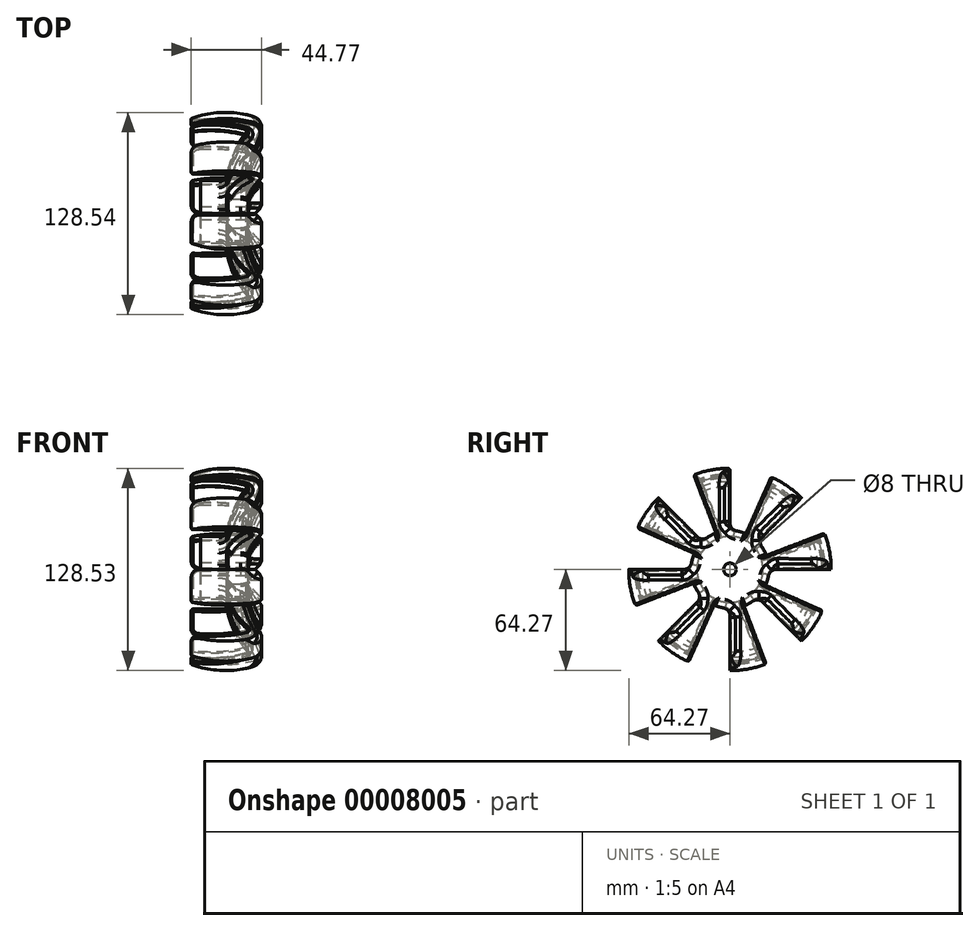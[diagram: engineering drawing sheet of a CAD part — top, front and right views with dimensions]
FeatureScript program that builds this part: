
annotation { "Feature Type Name" : "Feature", "Feature Type Description" : "" }
export const myFeature = defineFeature(function(context is Context, id is Id, definition is map)
    precondition{}
    {
        {
            var Q0;
            Q0=qCreatedBy(makeId("Front.planeOp"),FACE);
            var sketch = newSketch(context, id + "F0", { "sketchPlane" : qUnion([Q0])});
            skLineSegment(sketch, "E0", {"start": v(-28.32, 0) * mm, "end": v(30.34, 0) * mm, "construction": true});
            skLineSegment(sketch, "E1", {"start": v(-40.15, 4) * mm, "end": v(-10.15, 4) * mm});
            skLineSegment(sketch, "E2", {"start": v(-10.15, 4) * mm, "end": v(-10.15, 9.48) * mm});
            skLineSegment(sketch, "E3", {"start": v(-45.9, 60.38) * mm, "end": v(-45.9, 58.04) * mm});
            skLineSegment(sketch, "E4", {"start": v(-23.9, 20.95) * mm, "end": v(-40.15, 20.95) * mm});
            skLineSegment(sketch, "E5", {"start": v(-40.15, 20.95) * mm, "end": v(-40.15, 4) * mm});
            skArc(sketch, "E6", {"start": v(-6.27, 61.72) * mm, "mid": v(-26.2, 64.23) * mm, "end": v(-45.9, 60.38) * mm});
            skArc(sketch, "E7", {"start": v(-1.68, 52.13) * mm, "mid": v(-1.84, 57.95) * mm, "end": v(-6.27, 61.72) * mm});
            skArc(sketch, "E8", {"start": v(-1.68, 52.13) * mm, "mid": v(-8.01, 31.22) * mm, "end": v(-10.15, 9.48) * mm});
            skArc(sketch, "E9", {"start": v(-10.3, 52.56) * mm, "mid": v(-19.4, 37.75) * mm, "end": v(-23.9, 20.95) * mm});
            skArc(sketch, "E10", {"start": v(-10.98, 55.75) * mm, "mid": v(-28.31, 58.92) * mm, "end": v(-45.9, 58.04) * mm});
            skArc(sketch, "E11", {"start": v(-10.3, 52.56) * mm, "mid": v(-9.75, 54.35) * mm, "end": v(-10.98, 55.75) * mm});
            skSolve(sketch);
        }
        {
            var Q0;
            Q0 = qSketchRegion(id + "F0", true);
            var Q1;
            Q1=sQuery(id+"F0.wireOp",EDGE,"E0");
            revolve(context, id + "F1", {"entities" : qUnion([Q0]), "axis" : qUnion([Q1]), "revolveType" : RevolveType.FULL});
        }
        {
            var Q0;
            Q0=qCreatedBy(makeId("Right.planeOp"),FACE);
            var sketch = newSketch(context, id + "F2", { "sketchPlane" : qUnion([Q0])});
            skCircle(sketch, "E12", {"center": v(0, 0) * mm, "radius": 24.84 * mm});
            skLineSegment(sketch, "E13", {"start": v(0, 0) * mm, "end": v(0, 69.26) * mm});
            skLineSegment(sketch, "E14", {"start": v(0, 69.26) * mm, "end": v(29.19, 65.55) * mm});
            skLineSegment(sketch, "E15", {"start": v(29.19, 65.55) * mm, "end": v(0, 0) * mm});
            skLineSegment(sketch, "E16.1.0", {"start": v(-48.97, 48.97) * mm, "end": v(-25.72, 67) * mm});
            skLineSegment(sketch, "E16.1.1", {"start": v(-25.72, 67) * mm, "end": v(0, 0) * mm});
            skLineSegment(sketch, "E16.1.2", {"start": v(0, 0) * mm, "end": v(-48.97, 48.97) * mm});
            skLineSegment(sketch, "E16.2.0", {"start": v(-69.26, 0) * mm, "end": v(-65.55, 29.19) * mm});
            skLineSegment(sketch, "E16.2.1", {"start": v(-65.55, 29.19) * mm, "end": v(0, 0) * mm});
            skLineSegment(sketch, "E16.2.2", {"start": v(0, 0) * mm, "end": v(-69.26, 0) * mm});
            skLineSegment(sketch, "E17.1.3.0", {"start": v(-48.97, -48.97) * mm, "end": v(-67, -25.72) * mm});
            skLineSegment(sketch, "E17.3.3.0", {"start": v(-67, -25.72) * mm, "end": v(0, 0) * mm});
            skLineSegment(sketch, "E17.6.3.0", {"start": v(0, 0) * mm, "end": v(-48.97, -48.97) * mm});
            skLineSegment(sketch, "E17.1.4.0", {"start": v(0, -69.26) * mm, "end": v(-29.19, -65.55) * mm});
            skLineSegment(sketch, "E17.3.4.0", {"start": v(-29.19, -65.55) * mm, "end": v(0, 0) * mm});
            skLineSegment(sketch, "E17.6.4.0", {"start": v(0, 0) * mm, "end": v(0, -69.26) * mm});
            skLineSegment(sketch, "E17.1.5.0", {"start": v(48.97, -48.97) * mm, "end": v(25.72, -67) * mm});
            skLineSegment(sketch, "E17.3.5.0", {"start": v(25.72, -67) * mm, "end": v(0, 0) * mm});
            skLineSegment(sketch, "E17.6.5.0", {"start": v(0, 0) * mm, "end": v(48.97, -48.97) * mm});
            skLineSegment(sketch, "E17.1.6.0", {"start": v(69.26, 0) * mm, "end": v(65.55, -29.19) * mm});
            skLineSegment(sketch, "E17.3.6.0", {"start": v(65.55, -29.19) * mm, "end": v(0, 0) * mm});
            skLineSegment(sketch, "E17.6.6.0", {"start": v(0, 0) * mm, "end": v(69.26, 0) * mm});
            skLineSegment(sketch, "E17.1.7.0", {"start": v(48.97, 48.97) * mm, "end": v(67, 25.72) * mm});
            skLineSegment(sketch, "E17.3.7.0", {"start": v(67, 25.72) * mm, "end": v(0, 0) * mm});
            skLineSegment(sketch, "E17.6.7.0", {"start": v(0, 0) * mm, "end": v(48.97, 48.97) * mm});
            skSolve(sketch);
        }
        {
            var Q0;
            {var subQ3=sQuery(id+"F2.wireOp",EDGE,"E14");Q0=makeQuery(id+"F2.imprint","IMPRINT",FACE,{"disambiguationData":[TD([[makeQuery(id+"F2.imprint","IMPRINT",EDGE,{"derivedFrom":subQ3}),-1.0]])]});}
            var Q1;
            {var subQ3=sQuery(id+"F2.wireOp",EDGE,"E16.2.0");Q1=makeQuery(id+"F2.imprint","IMPRINT",FACE,{"disambiguationData":[TD([[makeQuery(id+"F2.imprint","IMPRINT",EDGE,{"derivedFrom":subQ3}),-1.0]])]});}
            var Q2;
            {var subQ3=sQuery(id+"F2.wireOp",EDGE,"E16.1.0");Q2=makeQuery(id+"F2.imprint","IMPRINT",FACE,{"disambiguationData":[TD([[makeQuery(id+"F2.imprint","IMPRINT",EDGE,{"derivedFrom":subQ3}),-1.0]])]});}
            var Q3;
            {var subQ3=sQuery(id+"F2.wireOp",EDGE,"E17.1.7.0");Q3=makeQuery(id+"F2.imprint","IMPRINT",FACE,{"disambiguationData":[TD([[makeQuery(id+"F2.imprint","IMPRINT",EDGE,{"derivedFrom":subQ3}),-1.0]])]});}
            var Q4;
            {var subQ3=sQuery(id+"F2.wireOp",EDGE,"E17.1.6.0");Q4=makeQuery(id+"F2.imprint","IMPRINT",FACE,{"disambiguationData":[TD([[makeQuery(id+"F2.imprint","IMPRINT",EDGE,{"derivedFrom":subQ3}),-1.0]])]});}
            var Q5;
            {var subQ3=sQuery(id+"F2.wireOp",EDGE,"E17.1.5.0");Q5=makeQuery(id+"F2.imprint","IMPRINT",FACE,{"disambiguationData":[TD([[makeQuery(id+"F2.imprint","IMPRINT",EDGE,{"derivedFrom":subQ3}),-1.0]])]});}
            var Q6;
            {var subQ3=sQuery(id+"F2.wireOp",EDGE,"E17.1.4.0");Q6=makeQuery(id+"F2.imprint","IMPRINT",FACE,{"disambiguationData":[TD([[makeQuery(id+"F2.imprint","IMPRINT",EDGE,{"derivedFrom":subQ3}),-1.0]])]});}
            var Q7;
            {var subQ3=sQuery(id+"F2.wireOp",EDGE,"E17.1.3.0");Q7=makeQuery(id+"F2.imprint","IMPRINT",FACE,{"disambiguationData":[TD([[makeQuery(id+"F2.imprint","IMPRINT",EDGE,{"derivedFrom":subQ3}),-1.0]])]});}
            extrude(context, id + "F3", {"entities" : qUnion([Q0, Q1, Q2, Q3, Q4, Q5, Q6, Q7]), "operationType" : NewBodyOperationType.REMOVE, "endBound" : BoundingType.THROUGH_ALL, "oppositeDirection" : true, "depth" : 25 * mm});
        }
        {
            var Q0;
            Q0=makeQuery(id+"F3.boolean.opBoolean","INTERSECT",EDGE,{"derivedFrom":[makeQuery(id+"F1.opRevolve","SWEPT_FACE",FACE,{"disambiguationData":[OSD([sQuery(id+"F0.wireOp",EDGE,"E8")])]}),makeQuery(id+"F3.opExtrude","SWEPT_FACE",FACE,{"disambiguationData":[OSD([sQuery(id+"F2.wireOp",EDGE,"E13")])]})]});
            var Q1;
            Q1=makeQuery(id+"F3.boolean.opBoolean","INTERSECT",EDGE,{"derivedFrom":[makeQuery(id+"F1.opRevolve","SWEPT_FACE",FACE,{"disambiguationData":[OSD([sQuery(id+"F0.wireOp",EDGE,"E8")])]}),makeQuery(id+"F3.opExtrude","SWEPT_FACE",FACE,{"disambiguationData":[OSD([sQuery(id+"F2.wireOp",EDGE,"E16.1.2")])]})]});
            var Q2;
            Q2=makeQuery(id+"F3.boolean.opBoolean","INTERSECT",EDGE,{"derivedFrom":[makeQuery(id+"F1.opRevolve","SWEPT_FACE",FACE,{"disambiguationData":[OSD([sQuery(id+"F0.wireOp",EDGE,"E8")])]}),makeQuery(id+"F3.opExtrude","SWEPT_FACE",FACE,{"disambiguationData":[OSD([sQuery(id+"F2.wireOp",EDGE,"E16.2.2")])]})]});
            var Q3;
            Q3=makeQuery(id+"F3.boolean.opBoolean","INTERSECT",EDGE,{"derivedFrom":[makeQuery(id+"F1.opRevolve","SWEPT_FACE",FACE,{"disambiguationData":[OSD([sQuery(id+"F0.wireOp",EDGE,"E8")])]}),makeQuery(id+"F3.opExtrude","SWEPT_FACE",FACE,{"disambiguationData":[OSD([sQuery(id+"F2.wireOp",EDGE,"E17.6.3.0")])]})]});
            var Q4;
            Q4=makeQuery(id+"F3.boolean.opBoolean","INTERSECT",EDGE,{"derivedFrom":[makeQuery(id+"F1.opRevolve","SWEPT_FACE",FACE,{"disambiguationData":[OSD([sQuery(id+"F0.wireOp",EDGE,"E8")])]}),makeQuery(id+"F3.opExtrude","SWEPT_FACE",FACE,{"disambiguationData":[OSD([sQuery(id+"F2.wireOp",EDGE,"E17.6.4.0")])]})]});
            var Q5;
            Q5=makeQuery(id+"F3.boolean.opBoolean","INTERSECT",EDGE,{"derivedFrom":[makeQuery(id+"F1.opRevolve","SWEPT_FACE",FACE,{"disambiguationData":[OSD([sQuery(id+"F0.wireOp",EDGE,"E8")])]}),makeQuery(id+"F3.opExtrude","SWEPT_FACE",FACE,{"disambiguationData":[OSD([sQuery(id+"F2.wireOp",EDGE,"E17.6.5.0")])]})]});
            var Q6;
            Q6=makeQuery(id+"F3.boolean.opBoolean","INTERSECT",EDGE,{"derivedFrom":[makeQuery(id+"F1.opRevolve","SWEPT_FACE",FACE,{"disambiguationData":[OSD([sQuery(id+"F0.wireOp",EDGE,"E8")])]}),makeQuery(id+"F3.opExtrude","SWEPT_FACE",FACE,{"disambiguationData":[OSD([sQuery(id+"F2.wireOp",EDGE,"E17.6.6.0")])]})]});
            var Q7;
            Q7=makeQuery(id+"F3.boolean.opBoolean","INTERSECT",EDGE,{"derivedFrom":[makeQuery(id+"F1.opRevolve","SWEPT_FACE",FACE,{"disambiguationData":[OSD([sQuery(id+"F0.wireOp",EDGE,"E8")])]}),makeQuery(id+"F3.opExtrude","SWEPT_FACE",FACE,{"disambiguationData":[OSD([sQuery(id+"F2.wireOp",EDGE,"E17.6.7.0")])]})]});
            chamfer(context, id + "F4", {"entities" : qUnion([Q0, Q1, Q2, Q3, Q4, Q5, Q6, Q7]), "width" : 5 * mm});
        }
        {
            var Q0;
            Q0=makeQuery(id+"F3.boolean.opBoolean","COPY",EDGE,{"derivedFrom":makeQuery(id+"F3.opExtrude","SWEPT_EDGE",EDGE,{"disambiguationData":[OSD([sQuery(id+"F2.wireOp",EDGE,"E12"),sQuery(id+"F2.wireOp",EDGE,"E17.6.7.0")])]})});
            var Q1;
            {var subQ0=sQuery(id+"F2.wireOp",EDGE,"E17.6.7.0");var subQ1=sQuery(id+"F2.wireOp",EDGE,"E12");Q1=makeQuery(id+"F4.opChamfer","BLEND_EDGE",EDGE,{"blendedFrom":[makeQuery(id+"F3.boolean.opBoolean","INTERSECT",EDGE,{"derivedFrom":[makeQuery(id+"F1.opRevolve","SWEPT_FACE",FACE,{"disambiguationData":[OSD([sQuery(id+"F0.wireOp",EDGE,"E8")])]}),makeQuery(id+"F3.opExtrude","SWEPT_FACE",FACE,{"disambiguationData":[OSD([subQ0])]})]}),makeQuery(id+"F3.boolean.opBoolean","COPY",FACE,{"derivedFrom":makeQuery(id+"F3.opExtrude","SWEPT_FACE",FACE,{"disambiguationData":[OSD([subQ1]),TDD([makeQuery(id+"F2.imprint","IMPRINT",EDGE,{"disambiguationData":[TD([[makeQuery(id+"F2.imprint","INTERSECT",VERTEX,{"derivedFrom":[subQ1,sQuery(id+"F2.wireOp",EDGE,"E17.3.7.0")]}),-1.0]])],"derivedFrom":subQ1})])]})})],"blendedInto":[makeQuery(id+"F3.boolean.opBoolean","COPY",FACE,{"derivedFrom":makeQuery(id+"F3.opExtrude","SWEPT_FACE",FACE,{"disambiguationData":[OSD([subQ1]),TDD([makeQuery(id+"F2.imprint","IMPRINT",EDGE,{"disambiguationData":[TD([[makeQuery(id+"F2.imprint","INTERSECT",VERTEX,{"derivedFrom":[subQ1,sQuery(id+"F2.wireOp",EDGE,"E17.3.7.0")]}),-1.0]])],"derivedFrom":subQ1})])]})})]});}
            var Q2;
            {var subQ0=sQuery(id+"F2.wireOp",EDGE,"E17.6.6.0");var subQ1=sQuery(id+"F2.wireOp",EDGE,"E12");Q2=makeQuery(id+"F4.opChamfer","BLEND_EDGE",EDGE,{"blendedFrom":[makeQuery(id+"F3.boolean.opBoolean","INTERSECT",EDGE,{"derivedFrom":[makeQuery(id+"F1.opRevolve","SWEPT_FACE",FACE,{"disambiguationData":[OSD([sQuery(id+"F0.wireOp",EDGE,"E8")])]}),makeQuery(id+"F3.opExtrude","SWEPT_FACE",FACE,{"disambiguationData":[OSD([subQ0])]})]}),makeQuery(id+"F3.boolean.opBoolean","COPY",FACE,{"derivedFrom":makeQuery(id+"F3.opExtrude","SWEPT_FACE",FACE,{"disambiguationData":[OSD([subQ1]),TDD([makeQuery(id+"F2.imprint","IMPRINT",EDGE,{"disambiguationData":[TD([[makeQuery(id+"F2.imprint","INTERSECT",VERTEX,{"derivedFrom":[subQ1,subQ0]}),1.0]])],"derivedFrom":subQ1})])]})})],"blendedInto":[makeQuery(id+"F3.boolean.opBoolean","COPY",FACE,{"derivedFrom":makeQuery(id+"F3.opExtrude","SWEPT_FACE",FACE,{"disambiguationData":[OSD([subQ1]),TDD([makeQuery(id+"F2.imprint","IMPRINT",EDGE,{"disambiguationData":[TD([[makeQuery(id+"F2.imprint","INTERSECT",VERTEX,{"derivedFrom":[subQ1,subQ0]}),1.0]])],"derivedFrom":subQ1})])]})})]});}
            var Q3;
            Q3=makeQuery(id+"F3.boolean.opBoolean","COPY",EDGE,{"derivedFrom":makeQuery(id+"F3.opExtrude","SWEPT_EDGE",EDGE,{"disambiguationData":[OSD([sQuery(id+"F2.wireOp",EDGE,"E12"),sQuery(id+"F2.wireOp",EDGE,"E17.6.6.0")])]})});
            var Q4;
            {var subQ0=sQuery(id+"F2.wireOp",EDGE,"E17.6.5.0");var subQ1=sQuery(id+"F2.wireOp",EDGE,"E12");Q4=makeQuery(id+"F4.opChamfer","BLEND_EDGE",EDGE,{"blendedFrom":[makeQuery(id+"F3.boolean.opBoolean","INTERSECT",EDGE,{"derivedFrom":[makeQuery(id+"F1.opRevolve","SWEPT_FACE",FACE,{"disambiguationData":[OSD([sQuery(id+"F0.wireOp",EDGE,"E8")])]}),makeQuery(id+"F3.opExtrude","SWEPT_FACE",FACE,{"disambiguationData":[OSD([subQ0])]})]}),makeQuery(id+"F3.boolean.opBoolean","COPY",FACE,{"derivedFrom":makeQuery(id+"F3.opExtrude","SWEPT_FACE",FACE,{"disambiguationData":[OSD([subQ1]),TDD([makeQuery(id+"F2.imprint","IMPRINT",EDGE,{"disambiguationData":[TD([[makeQuery(id+"F2.imprint","INTERSECT",VERTEX,{"derivedFrom":[subQ1,sQuery(id+"F2.wireOp",EDGE,"E17.3.5.0")]}),-1.0]])],"derivedFrom":subQ1})])]})})],"blendedInto":[makeQuery(id+"F3.boolean.opBoolean","COPY",FACE,{"derivedFrom":makeQuery(id+"F3.opExtrude","SWEPT_FACE",FACE,{"disambiguationData":[OSD([subQ1]),TDD([makeQuery(id+"F2.imprint","IMPRINT",EDGE,{"disambiguationData":[TD([[makeQuery(id+"F2.imprint","INTERSECT",VERTEX,{"derivedFrom":[subQ1,sQuery(id+"F2.wireOp",EDGE,"E17.3.5.0")]}),-1.0]])],"derivedFrom":subQ1})])]})})]});}
            var Q5;
            Q5=makeQuery(id+"F3.boolean.opBoolean","COPY",EDGE,{"derivedFrom":makeQuery(id+"F3.opExtrude","SWEPT_EDGE",EDGE,{"disambiguationData":[OSD([sQuery(id+"F2.wireOp",EDGE,"E12"),sQuery(id+"F2.wireOp",EDGE,"E17.6.5.0")])]})});
            var Q6;
            {var subQ0=sQuery(id+"F2.wireOp",EDGE,"E17.6.4.0");var subQ1=sQuery(id+"F2.wireOp",EDGE,"E12");Q6=makeQuery(id+"F4.opChamfer","BLEND_EDGE",EDGE,{"blendedFrom":[makeQuery(id+"F3.boolean.opBoolean","INTERSECT",EDGE,{"derivedFrom":[makeQuery(id+"F1.opRevolve","SWEPT_FACE",FACE,{"disambiguationData":[OSD([sQuery(id+"F0.wireOp",EDGE,"E8")])]}),makeQuery(id+"F3.opExtrude","SWEPT_FACE",FACE,{"disambiguationData":[OSD([subQ0])]})]}),makeQuery(id+"F3.boolean.opBoolean","COPY",FACE,{"derivedFrom":makeQuery(id+"F3.opExtrude","SWEPT_FACE",FACE,{"disambiguationData":[OSD([subQ1]),TDD([makeQuery(id+"F2.imprint","IMPRINT",EDGE,{"disambiguationData":[TD([[makeQuery(id+"F2.imprint","INTERSECT",VERTEX,{"derivedFrom":[subQ1,sQuery(id+"F2.wireOp",EDGE,"E17.3.4.0")]}),-1.0]])],"derivedFrom":subQ1})])]})})],"blendedInto":[makeQuery(id+"F3.boolean.opBoolean","COPY",FACE,{"derivedFrom":makeQuery(id+"F3.opExtrude","SWEPT_FACE",FACE,{"disambiguationData":[OSD([subQ1]),TDD([makeQuery(id+"F2.imprint","IMPRINT",EDGE,{"disambiguationData":[TD([[makeQuery(id+"F2.imprint","INTERSECT",VERTEX,{"derivedFrom":[subQ1,sQuery(id+"F2.wireOp",EDGE,"E17.3.4.0")]}),-1.0]])],"derivedFrom":subQ1})])]})})]});}
            var Q7;
            Q7=makeQuery(id+"F3.boolean.opBoolean","COPY",EDGE,{"derivedFrom":makeQuery(id+"F3.opExtrude","SWEPT_EDGE",EDGE,{"disambiguationData":[OSD([sQuery(id+"F2.wireOp",EDGE,"E12"),sQuery(id+"F2.wireOp",EDGE,"E17.6.4.0")])]})});
            var Q8;
            {var subQ0=sQuery(id+"F2.wireOp",EDGE,"E17.6.3.0");var subQ1=sQuery(id+"F2.wireOp",EDGE,"E12");Q8=makeQuery(id+"F4.opChamfer","BLEND_EDGE",EDGE,{"blendedFrom":[makeQuery(id+"F3.boolean.opBoolean","INTERSECT",EDGE,{"derivedFrom":[makeQuery(id+"F1.opRevolve","SWEPT_FACE",FACE,{"disambiguationData":[OSD([sQuery(id+"F0.wireOp",EDGE,"E8")])]}),makeQuery(id+"F3.opExtrude","SWEPT_FACE",FACE,{"disambiguationData":[OSD([subQ0])]})]}),makeQuery(id+"F3.boolean.opBoolean","COPY",FACE,{"derivedFrom":makeQuery(id+"F3.opExtrude","SWEPT_FACE",FACE,{"disambiguationData":[OSD([subQ1]),TDD([makeQuery(id+"F2.imprint","IMPRINT",EDGE,{"disambiguationData":[TD([[makeQuery(id+"F2.imprint","INTERSECT",VERTEX,{"derivedFrom":[subQ1,sQuery(id+"F2.wireOp",EDGE,"E17.3.3.0")]}),-1.0]])],"derivedFrom":subQ1})])]})})],"blendedInto":[makeQuery(id+"F3.boolean.opBoolean","COPY",FACE,{"derivedFrom":makeQuery(id+"F3.opExtrude","SWEPT_FACE",FACE,{"disambiguationData":[OSD([subQ1]),TDD([makeQuery(id+"F2.imprint","IMPRINT",EDGE,{"disambiguationData":[TD([[makeQuery(id+"F2.imprint","INTERSECT",VERTEX,{"derivedFrom":[subQ1,sQuery(id+"F2.wireOp",EDGE,"E17.3.3.0")]}),-1.0]])],"derivedFrom":subQ1})])]})})]});}
            var Q9;
            Q9=makeQuery(id+"F3.boolean.opBoolean","COPY",EDGE,{"derivedFrom":makeQuery(id+"F3.opExtrude","SWEPT_EDGE",EDGE,{"disambiguationData":[OSD([sQuery(id+"F2.wireOp",EDGE,"E12"),sQuery(id+"F2.wireOp",EDGE,"E17.6.3.0")])]})});
            var Q10;
            {var subQ0=sQuery(id+"F2.wireOp",EDGE,"E16.2.2");var subQ1=sQuery(id+"F2.wireOp",EDGE,"E12");Q10=makeQuery(id+"F4.opChamfer","BLEND_EDGE",EDGE,{"blendedFrom":[makeQuery(id+"F3.boolean.opBoolean","INTERSECT",EDGE,{"derivedFrom":[makeQuery(id+"F1.opRevolve","SWEPT_FACE",FACE,{"disambiguationData":[OSD([sQuery(id+"F0.wireOp",EDGE,"E8")])]}),makeQuery(id+"F3.opExtrude","SWEPT_FACE",FACE,{"disambiguationData":[OSD([subQ0])]})]}),makeQuery(id+"F3.boolean.opBoolean","COPY",FACE,{"derivedFrom":makeQuery(id+"F3.opExtrude","SWEPT_FACE",FACE,{"disambiguationData":[OSD([subQ1]),TDD([makeQuery(id+"F2.imprint","IMPRINT",EDGE,{"disambiguationData":[TD([[makeQuery(id+"F2.imprint","INTERSECT",VERTEX,{"derivedFrom":[subQ1,sQuery(id+"F2.wireOp",EDGE,"E16.2.1")]}),-1.0]])],"derivedFrom":subQ1})])]})})],"blendedInto":[makeQuery(id+"F3.boolean.opBoolean","COPY",FACE,{"derivedFrom":makeQuery(id+"F3.opExtrude","SWEPT_FACE",FACE,{"disambiguationData":[OSD([subQ1]),TDD([makeQuery(id+"F2.imprint","IMPRINT",EDGE,{"disambiguationData":[TD([[makeQuery(id+"F2.imprint","INTERSECT",VERTEX,{"derivedFrom":[subQ1,sQuery(id+"F2.wireOp",EDGE,"E16.2.1")]}),-1.0]])],"derivedFrom":subQ1})])]})})]});}
            var Q11;
            Q11=makeQuery(id+"F3.boolean.opBoolean","COPY",EDGE,{"derivedFrom":makeQuery(id+"F3.opExtrude","SWEPT_EDGE",EDGE,{"disambiguationData":[OSD([sQuery(id+"F2.wireOp",EDGE,"E12"),sQuery(id+"F2.wireOp",EDGE,"E16.2.2")])]})});
            var Q12;
            Q12=makeQuery(id+"F3.boolean.opBoolean","COPY",EDGE,{"derivedFrom":makeQuery(id+"F3.opExtrude","SWEPT_EDGE",EDGE,{"disambiguationData":[OSD([sQuery(id+"F2.wireOp",EDGE,"E12"),sQuery(id+"F2.wireOp",EDGE,"E16.1.2")])]})});
            var Q13;
            {var subQ0=sQuery(id+"F2.wireOp",EDGE,"E16.1.2");var subQ1=sQuery(id+"F2.wireOp",EDGE,"E12");Q13=makeQuery(id+"F4.opChamfer","BLEND_EDGE",EDGE,{"blendedFrom":[makeQuery(id+"F3.boolean.opBoolean","INTERSECT",EDGE,{"derivedFrom":[makeQuery(id+"F1.opRevolve","SWEPT_FACE",FACE,{"disambiguationData":[OSD([sQuery(id+"F0.wireOp",EDGE,"E8")])]}),makeQuery(id+"F3.opExtrude","SWEPT_FACE",FACE,{"disambiguationData":[OSD([subQ0])]})]}),makeQuery(id+"F3.boolean.opBoolean","COPY",FACE,{"derivedFrom":makeQuery(id+"F3.opExtrude","SWEPT_FACE",FACE,{"disambiguationData":[OSD([subQ1]),TDD([makeQuery(id+"F2.imprint","IMPRINT",EDGE,{"disambiguationData":[TD([[makeQuery(id+"F2.imprint","INTERSECT",VERTEX,{"derivedFrom":[subQ1,sQuery(id+"F2.wireOp",EDGE,"E16.1.1")]}),-1.0]])],"derivedFrom":subQ1})])]})})],"blendedInto":[makeQuery(id+"F3.boolean.opBoolean","COPY",FACE,{"derivedFrom":makeQuery(id+"F3.opExtrude","SWEPT_FACE",FACE,{"disambiguationData":[OSD([subQ1]),TDD([makeQuery(id+"F2.imprint","IMPRINT",EDGE,{"disambiguationData":[TD([[makeQuery(id+"F2.imprint","INTERSECT",VERTEX,{"derivedFrom":[subQ1,sQuery(id+"F2.wireOp",EDGE,"E16.1.1")]}),-1.0]])],"derivedFrom":subQ1})])]})})]});}
            var Q14;
            Q14=makeQuery(id+"F3.boolean.opBoolean","COPY",EDGE,{"derivedFrom":makeQuery(id+"F3.opExtrude","SWEPT_EDGE",EDGE,{"disambiguationData":[OSD([sQuery(id+"F2.wireOp",EDGE,"E12"),sQuery(id+"F2.wireOp",EDGE,"E13")])]})});
            var Q15;
            {var subQ0=sQuery(id+"F2.wireOp",EDGE,"E13");var subQ1=sQuery(id+"F2.wireOp",EDGE,"E12");Q15=makeQuery(id+"F4.opChamfer","BLEND_EDGE",EDGE,{"blendedFrom":[makeQuery(id+"F3.boolean.opBoolean","INTERSECT",EDGE,{"derivedFrom":[makeQuery(id+"F1.opRevolve","SWEPT_FACE",FACE,{"disambiguationData":[OSD([sQuery(id+"F0.wireOp",EDGE,"E8")])]}),makeQuery(id+"F3.opExtrude","SWEPT_FACE",FACE,{"disambiguationData":[OSD([subQ0])]})]}),makeQuery(id+"F3.boolean.opBoolean","COPY",FACE,{"derivedFrom":makeQuery(id+"F3.opExtrude","SWEPT_FACE",FACE,{"disambiguationData":[OSD([subQ1]),TDD([makeQuery(id+"F2.imprint","IMPRINT",EDGE,{"disambiguationData":[TD([[makeQuery(id+"F2.imprint","INTERSECT",VERTEX,{"derivedFrom":[subQ1,sQuery(id+"F2.wireOp",EDGE,"E15")]}),-1.0]])],"derivedFrom":subQ1})])]})})],"blendedInto":[makeQuery(id+"F3.boolean.opBoolean","COPY",FACE,{"derivedFrom":makeQuery(id+"F3.opExtrude","SWEPT_FACE",FACE,{"disambiguationData":[OSD([subQ1]),TDD([makeQuery(id+"F2.imprint","IMPRINT",EDGE,{"disambiguationData":[TD([[makeQuery(id+"F2.imprint","INTERSECT",VERTEX,{"derivedFrom":[subQ1,sQuery(id+"F2.wireOp",EDGE,"E15")]}),-1.0]])],"derivedFrom":subQ1})])]})})]});}
            fillet(context, id + "F5", {"entities" : qUnion([Q0, Q1, Q2, Q3, Q4, Q5, Q6, Q7, Q8, Q9, Q10, Q11, Q12, Q13, Q14, Q15]), "radius" : 5 * mm, "tangentPropagation" : true, "allowEdgeOverflow" : false});
        }
        {
            var Q0;
            Q0=makeQuery(id+"F3.boolean.opBoolean","INTERSECT",EDGE,{"derivedFrom":[makeQuery(id+"F1.opRevolve","SWEPT_FACE",FACE,{"disambiguationData":[OSD([sQuery(id+"F0.wireOp",EDGE,"E9")])]}),makeQuery(id+"F3.opExtrude","SWEPT_FACE",FACE,{"disambiguationData":[OSD([sQuery(id+"F2.wireOp",EDGE,"E16.2.1")])]})]});
            var Q1;
            Q1=makeQuery(id+"F3.boolean.opBoolean","INTERSECT",EDGE,{"derivedFrom":[makeQuery(id+"F1.opRevolve","SWEPT_FACE",FACE,{"disambiguationData":[OSD([sQuery(id+"F0.wireOp",EDGE,"E10")])]}),makeQuery(id+"F3.opExtrude","SWEPT_FACE",FACE,{"disambiguationData":[OSD([sQuery(id+"F2.wireOp",EDGE,"E16.2.1")])]})]});
            var Q2;
            Q2=makeQuery(id+"F3.boolean.opBoolean","INTERSECT",EDGE,{"derivedFrom":[makeQuery(id+"F1.opRevolve","SWEPT_FACE",FACE,{"disambiguationData":[OSD([sQuery(id+"F0.wireOp",EDGE,"E11")])]}),makeQuery(id+"F3.opExtrude","SWEPT_FACE",FACE,{"disambiguationData":[OSD([sQuery(id+"F2.wireOp",EDGE,"E16.2.1")])]})]});
            var Q3;
            Q3=makeQuery(id+"F3.boolean.opBoolean","INTERSECT",EDGE,{"derivedFrom":[makeQuery(id+"F1.opRevolve","SWEPT_FACE",FACE,{"disambiguationData":[OSD([sQuery(id+"F0.wireOp",EDGE,"E9")])]}),makeQuery(id+"F3.opExtrude","SWEPT_FACE",FACE,{"disambiguationData":[OSD([sQuery(id+"F2.wireOp",EDGE,"E17.3.3.0")])]})]});
            var Q4;
            Q4=makeQuery(id+"F3.boolean.opBoolean","INTERSECT",EDGE,{"derivedFrom":[makeQuery(id+"F1.opRevolve","SWEPT_FACE",FACE,{"disambiguationData":[OSD([sQuery(id+"F0.wireOp",EDGE,"E11")])]}),makeQuery(id+"F3.opExtrude","SWEPT_FACE",FACE,{"disambiguationData":[OSD([sQuery(id+"F2.wireOp",EDGE,"E17.3.3.0")])]})]});
            var Q5;
            Q5=makeQuery(id+"F3.boolean.opBoolean","INTERSECT",EDGE,{"derivedFrom":[makeQuery(id+"F1.opRevolve","SWEPT_FACE",FACE,{"disambiguationData":[OSD([sQuery(id+"F0.wireOp",EDGE,"E10")])]}),makeQuery(id+"F3.opExtrude","SWEPT_FACE",FACE,{"disambiguationData":[OSD([sQuery(id+"F2.wireOp",EDGE,"E17.3.3.0")])]})]});
            var Q6;
            Q6=makeQuery(id+"F3.boolean.opBoolean","INTERSECT",EDGE,{"derivedFrom":[makeQuery(id+"F1.opRevolve","SWEPT_FACE",FACE,{"disambiguationData":[OSD([sQuery(id+"F0.wireOp",EDGE,"E9")])]}),makeQuery(id+"F3.opExtrude","SWEPT_FACE",FACE,{"disambiguationData":[OSD([sQuery(id+"F2.wireOp",EDGE,"E17.3.4.0")])]})]});
            var Q7;
            Q7=makeQuery(id+"F3.boolean.opBoolean","INTERSECT",EDGE,{"derivedFrom":[makeQuery(id+"F1.opRevolve","SWEPT_FACE",FACE,{"disambiguationData":[OSD([sQuery(id+"F0.wireOp",EDGE,"E10")])]}),makeQuery(id+"F3.opExtrude","SWEPT_FACE",FACE,{"disambiguationData":[OSD([sQuery(id+"F2.wireOp",EDGE,"E17.3.4.0")])]})]});
            var Q8;
            Q8=makeQuery(id+"F3.boolean.opBoolean","INTERSECT",EDGE,{"derivedFrom":[makeQuery(id+"F1.opRevolve","SWEPT_FACE",FACE,{"disambiguationData":[OSD([sQuery(id+"F0.wireOp",EDGE,"E10")])]}),makeQuery(id+"F3.opExtrude","SWEPT_FACE",FACE,{"disambiguationData":[OSD([sQuery(id+"F2.wireOp",EDGE,"E17.3.5.0")])]})]});
            var Q9;
            Q9=makeQuery(id+"F3.boolean.opBoolean","INTERSECT",EDGE,{"derivedFrom":[makeQuery(id+"F1.opRevolve","SWEPT_FACE",FACE,{"disambiguationData":[OSD([sQuery(id+"F0.wireOp",EDGE,"E9")])]}),makeQuery(id+"F3.opExtrude","SWEPT_FACE",FACE,{"disambiguationData":[OSD([sQuery(id+"F2.wireOp",EDGE,"E17.3.5.0")])]})]});
            var Q10;
            Q10=makeQuery(id+"F3.boolean.opBoolean","INTERSECT",EDGE,{"derivedFrom":[makeQuery(id+"F1.opRevolve","SWEPT_FACE",FACE,{"disambiguationData":[OSD([sQuery(id+"F0.wireOp",EDGE,"E9")])]}),makeQuery(id+"F3.opExtrude","SWEPT_FACE",FACE,{"disambiguationData":[OSD([sQuery(id+"F2.wireOp",EDGE,"E17.3.6.0")])]})]});
            var Q11;
            Q11=makeQuery(id+"F3.boolean.opBoolean","INTERSECT",EDGE,{"derivedFrom":[makeQuery(id+"F1.opRevolve","SWEPT_FACE",FACE,{"disambiguationData":[OSD([sQuery(id+"F0.wireOp",EDGE,"E10")])]}),makeQuery(id+"F3.opExtrude","SWEPT_FACE",FACE,{"disambiguationData":[OSD([sQuery(id+"F2.wireOp",EDGE,"E17.3.6.0")])]})]});
            var Q12;
            Q12=makeQuery(id+"F3.boolean.opBoolean","INTERSECT",EDGE,{"derivedFrom":[makeQuery(id+"F1.opRevolve","SWEPT_FACE",FACE,{"disambiguationData":[OSD([sQuery(id+"F0.wireOp",EDGE,"E9")])]}),makeQuery(id+"F3.opExtrude","SWEPT_FACE",FACE,{"disambiguationData":[OSD([sQuery(id+"F2.wireOp",EDGE,"E17.3.7.0")])]})]});
            var Q13;
            Q13=makeQuery(id+"F3.boolean.opBoolean","INTERSECT",EDGE,{"derivedFrom":[makeQuery(id+"F1.opRevolve","SWEPT_FACE",FACE,{"disambiguationData":[OSD([sQuery(id+"F0.wireOp",EDGE,"E10")])]}),makeQuery(id+"F3.opExtrude","SWEPT_FACE",FACE,{"disambiguationData":[OSD([sQuery(id+"F2.wireOp",EDGE,"E17.3.7.0")])]})]});
            var Q14;
            Q14=makeQuery(id+"F3.boolean.opBoolean","INTERSECT",EDGE,{"derivedFrom":[makeQuery(id+"F1.opRevolve","SWEPT_FACE",FACE,{"disambiguationData":[OSD([sQuery(id+"F0.wireOp",EDGE,"E9")])]}),makeQuery(id+"F3.opExtrude","SWEPT_FACE",FACE,{"disambiguationData":[OSD([sQuery(id+"F2.wireOp",EDGE,"E15")])]})]});
            var Q15;
            Q15=makeQuery(id+"F3.boolean.opBoolean","INTERSECT",EDGE,{"derivedFrom":[makeQuery(id+"F1.opRevolve","SWEPT_FACE",FACE,{"disambiguationData":[OSD([sQuery(id+"F0.wireOp",EDGE,"E10")])]}),makeQuery(id+"F3.opExtrude","SWEPT_FACE",FACE,{"disambiguationData":[OSD([sQuery(id+"F2.wireOp",EDGE,"E15")])]})]});
            var Q16;
            Q16=makeQuery(id+"F3.boolean.opBoolean","INTERSECT",EDGE,{"derivedFrom":[makeQuery(id+"F1.opRevolve","SWEPT_FACE",FACE,{"disambiguationData":[OSD([sQuery(id+"F0.wireOp",EDGE,"E9")])]}),makeQuery(id+"F3.opExtrude","SWEPT_FACE",FACE,{"disambiguationData":[OSD([sQuery(id+"F2.wireOp",EDGE,"E16.1.1")])]})]});
            var Q17;
            Q17=makeQuery(id+"F3.boolean.opBoolean","INTERSECT",EDGE,{"derivedFrom":[makeQuery(id+"F1.opRevolve","SWEPT_FACE",FACE,{"disambiguationData":[OSD([sQuery(id+"F0.wireOp",EDGE,"E10")])]}),makeQuery(id+"F3.opExtrude","SWEPT_FACE",FACE,{"disambiguationData":[OSD([sQuery(id+"F2.wireOp",EDGE,"E16.1.1")])]})]});
            var Q18;
            Q18=makeQuery(id+"F3.boolean.opBoolean","INTERSECT",EDGE,{"derivedFrom":[makeQuery(id+"F1.opRevolve","SWEPT_FACE",FACE,{"disambiguationData":[OSD([sQuery(id+"F0.wireOp",EDGE,"E11")])]}),makeQuery(id+"F3.opExtrude","SWEPT_FACE",FACE,{"disambiguationData":[OSD([sQuery(id+"F2.wireOp",EDGE,"E16.1.1")])]})]});
            chamfer(context, id + "F6", {"entities" : qUnion([Q0, Q1, Q2, Q3, Q4, Q5, Q6, Q7, Q8, Q9, Q10, Q11, Q12, Q13, Q14, Q15, Q16, Q17, Q18]), "width" : 3 * mm, "tangentPropagation" : true});
        }
        {
            var Q0;
            {var subQ0=makeQuery(id+"F1.opRevolve","SWEPT_FACE",FACE,{"disambiguationData":[OSD([sQuery(id+"F0.wireOp",EDGE,"E8")])]});Q0=makeQuery(id+"F4.opChamfer","BLEND_EDGE",EDGE,{"blendedFrom":[makeQuery(id+"F3.boolean.opBoolean","INTERSECT",EDGE,{"derivedFrom":[subQ0,makeQuery(id+"F3.opExtrude","SWEPT_FACE",FACE,{"disambiguationData":[OSD([sQuery(id+"F2.wireOp",EDGE,"E17.6.5.0")])]})]}),subQ0],"blendedInto":[subQ0]});}
            var Q1;
            {var subQ0=makeQuery(id+"F1.opRevolve","SWEPT_FACE",FACE,{"disambiguationData":[OSD([sQuery(id+"F0.wireOp",EDGE,"E8")])]});Q1=makeQuery(id+"F4.opChamfer","BLEND_EDGE",EDGE,{"blendedFrom":[makeQuery(id+"F3.boolean.opBoolean","INTERSECT",EDGE,{"derivedFrom":[subQ0,makeQuery(id+"F3.opExtrude","SWEPT_FACE",FACE,{"disambiguationData":[OSD([sQuery(id+"F2.wireOp",EDGE,"E17.6.4.0")])]})]}),subQ0],"blendedInto":[subQ0]});}
            var Q2;
            {var subQ0=makeQuery(id+"F1.opRevolve","SWEPT_FACE",FACE,{"disambiguationData":[OSD([sQuery(id+"F0.wireOp",EDGE,"E8")])]});Q2=makeQuery(id+"F4.opChamfer","BLEND_EDGE",EDGE,{"blendedFrom":[makeQuery(id+"F3.boolean.opBoolean","INTERSECT",EDGE,{"derivedFrom":[subQ0,makeQuery(id+"F3.opExtrude","SWEPT_FACE",FACE,{"disambiguationData":[OSD([sQuery(id+"F2.wireOp",EDGE,"E17.6.6.0")])]})]}),subQ0],"blendedInto":[subQ0]});}
            var Q3;
            {var subQ0=makeQuery(id+"F1.opRevolve","SWEPT_FACE",FACE,{"disambiguationData":[OSD([sQuery(id+"F0.wireOp",EDGE,"E8")])]});Q3=makeQuery(id+"F4.opChamfer","BLEND_EDGE",EDGE,{"blendedFrom":[makeQuery(id+"F3.boolean.opBoolean","INTERSECT",EDGE,{"derivedFrom":[subQ0,makeQuery(id+"F3.opExtrude","SWEPT_FACE",FACE,{"disambiguationData":[OSD([sQuery(id+"F2.wireOp",EDGE,"E17.6.7.0")])]})]}),subQ0],"blendedInto":[subQ0]});}
            var Q4;
            {var subQ0=makeQuery(id+"F1.opRevolve","SWEPT_FACE",FACE,{"disambiguationData":[OSD([sQuery(id+"F0.wireOp",EDGE,"E8")])]});Q4=makeQuery(id+"F4.opChamfer","BLEND_EDGE",EDGE,{"blendedFrom":[makeQuery(id+"F3.boolean.opBoolean","INTERSECT",EDGE,{"derivedFrom":[subQ0,makeQuery(id+"F3.opExtrude","SWEPT_FACE",FACE,{"disambiguationData":[OSD([sQuery(id+"F2.wireOp",EDGE,"E13")])]})]}),subQ0],"blendedInto":[subQ0]});}
            var Q5;
            {var subQ0=makeQuery(id+"F1.opRevolve","SWEPT_FACE",FACE,{"disambiguationData":[OSD([sQuery(id+"F0.wireOp",EDGE,"E8")])]});Q5=makeQuery(id+"F4.opChamfer","BLEND_EDGE",EDGE,{"blendedFrom":[makeQuery(id+"F3.boolean.opBoolean","INTERSECT",EDGE,{"derivedFrom":[subQ0,makeQuery(id+"F3.opExtrude","SWEPT_FACE",FACE,{"disambiguationData":[OSD([sQuery(id+"F2.wireOp",EDGE,"E16.1.2")])]})]}),subQ0],"blendedInto":[subQ0]});}
            var Q6;
            {var subQ0=makeQuery(id+"F1.opRevolve","SWEPT_FACE",FACE,{"disambiguationData":[OSD([sQuery(id+"F0.wireOp",EDGE,"E8")])]});Q6=makeQuery(id+"F4.opChamfer","BLEND_EDGE",EDGE,{"blendedFrom":[makeQuery(id+"F3.boolean.opBoolean","INTERSECT",EDGE,{"derivedFrom":[subQ0,makeQuery(id+"F3.opExtrude","SWEPT_FACE",FACE,{"disambiguationData":[OSD([sQuery(id+"F2.wireOp",EDGE,"E16.2.2")])]})]}),subQ0],"blendedInto":[subQ0]});}
            var Q7;
            {var subQ0=makeQuery(id+"F1.opRevolve","SWEPT_FACE",FACE,{"disambiguationData":[OSD([sQuery(id+"F0.wireOp",EDGE,"E8")])]});Q7=makeQuery(id+"F4.opChamfer","BLEND_EDGE",EDGE,{"blendedFrom":[makeQuery(id+"F3.boolean.opBoolean","INTERSECT",EDGE,{"derivedFrom":[subQ0,makeQuery(id+"F3.opExtrude","SWEPT_FACE",FACE,{"disambiguationData":[OSD([sQuery(id+"F2.wireOp",EDGE,"E17.6.3.0")])]})]}),subQ0],"blendedInto":[subQ0]});}
            fillet(context, id + "F7", {"entities" : qUnion([Q0, Q1, Q2, Q3, Q4, Q5, Q6, Q7]), "radius" : 5 * mm, "tangentPropagation" : true, "allowEdgeOverflow" : false});
        }
        {
            var Q0;
            Q0=makeQuery(id+"F3.boolean.opBoolean","INTERSECT",EDGE,{"derivedFrom":[makeQuery(id+"F1.opRevolve","SWEPT_FACE",FACE,{"disambiguationData":[OSD([sQuery(id+"F0.wireOp",EDGE,"E3")])]}),makeQuery(id+"F3.opExtrude","SWEPT_FACE",FACE,{"disambiguationData":[OSD([sQuery(id+"F2.wireOp",EDGE,"E17.6.6.0")])]})]});
            var Q1;
            Q1=makeQuery(id+"F3.boolean.opBoolean","INTERSECT",EDGE,{"derivedFrom":[makeQuery(id+"F1.opRevolve","SWEPT_FACE",FACE,{"disambiguationData":[OSD([sQuery(id+"F0.wireOp",EDGE,"E3")])]}),makeQuery(id+"F3.opExtrude","SWEPT_FACE",FACE,{"disambiguationData":[OSD([sQuery(id+"F2.wireOp",EDGE,"E17.6.5.0")])]})]});
            var Q2;
            Q2=makeQuery(id+"F3.boolean.opBoolean","INTERSECT",EDGE,{"derivedFrom":[makeQuery(id+"F1.opRevolve","SWEPT_FACE",FACE,{"disambiguationData":[OSD([sQuery(id+"F0.wireOp",EDGE,"E3")])]}),makeQuery(id+"F3.opExtrude","SWEPT_FACE",FACE,{"disambiguationData":[OSD([sQuery(id+"F2.wireOp",EDGE,"E17.6.4.0")])]})]});
            var Q3;
            Q3=makeQuery(id+"F3.boolean.opBoolean","INTERSECT",EDGE,{"derivedFrom":[makeQuery(id+"F1.opRevolve","SWEPT_FACE",FACE,{"disambiguationData":[OSD([sQuery(id+"F0.wireOp",EDGE,"E3")])]}),makeQuery(id+"F3.opExtrude","SWEPT_FACE",FACE,{"disambiguationData":[OSD([sQuery(id+"F2.wireOp",EDGE,"E17.6.3.0")])]})]});
            var Q4;
            Q4=makeQuery(id+"F3.boolean.opBoolean","INTERSECT",EDGE,{"derivedFrom":[makeQuery(id+"F1.opRevolve","SWEPT_FACE",FACE,{"disambiguationData":[OSD([sQuery(id+"F0.wireOp",EDGE,"E3")])]}),makeQuery(id+"F3.opExtrude","SWEPT_FACE",FACE,{"disambiguationData":[OSD([sQuery(id+"F2.wireOp",EDGE,"E16.2.2")])]})]});
            var Q5;
            Q5=makeQuery(id+"F3.boolean.opBoolean","INTERSECT",EDGE,{"derivedFrom":[makeQuery(id+"F1.opRevolve","SWEPT_FACE",FACE,{"disambiguationData":[OSD([sQuery(id+"F0.wireOp",EDGE,"E3")])]}),makeQuery(id+"F3.opExtrude","SWEPT_FACE",FACE,{"disambiguationData":[OSD([sQuery(id+"F2.wireOp",EDGE,"E16.1.2")])]})]});
            var Q6;
            Q6=makeQuery(id+"F3.boolean.opBoolean","INTERSECT",EDGE,{"derivedFrom":[makeQuery(id+"F1.opRevolve","SWEPT_FACE",FACE,{"disambiguationData":[OSD([sQuery(id+"F0.wireOp",EDGE,"E3")])]}),makeQuery(id+"F3.opExtrude","SWEPT_FACE",FACE,{"disambiguationData":[OSD([sQuery(id+"F2.wireOp",EDGE,"E13")])]})]});
            var Q7;
            Q7=makeQuery(id+"F3.boolean.opBoolean","INTERSECT",EDGE,{"derivedFrom":[makeQuery(id+"F1.opRevolve","SWEPT_FACE",FACE,{"disambiguationData":[OSD([sQuery(id+"F0.wireOp",EDGE,"E3")])]}),makeQuery(id+"F3.opExtrude","SWEPT_FACE",FACE,{"disambiguationData":[OSD([sQuery(id+"F2.wireOp",EDGE,"E17.6.7.0")])]})]});
            fillet(context, id + "F8", {"entities" : qUnion([Q0, Q1, Q2, Q3, Q4, Q5, Q6, Q7]), "radius" : 5 * mm, "tangentPropagation" : true, "allowEdgeOverflow" : false});
        }
        {
            var Q0;
            Q0=makeQuery(id+"F3.boolean.opBoolean","COPY",EDGE,{"derivedFrom":makeQuery(id+"F3.opExtrude","SWEPT_EDGE",EDGE,{"disambiguationData":[OSD([sQuery(id+"F2.wireOp",EDGE,"E12"),sQuery(id+"F2.wireOp",EDGE,"E17.3.5.0")])]})});
            var Q1;
            {var subQ0=sQuery(id+"F2.wireOp",EDGE,"E17.3.5.0");var subQ1=sQuery(id+"F2.wireOp",EDGE,"E12");Q1=makeQuery(id+"F6.opChamfer","BLEND_EDGE",EDGE,{"blendedFrom":[makeQuery(id+"F3.boolean.opBoolean","INTERSECT",EDGE,{"derivedFrom":[makeQuery(id+"F1.opRevolve","SWEPT_FACE",FACE,{"disambiguationData":[OSD([sQuery(id+"F0.wireOp",EDGE,"E9")])]}),makeQuery(id+"F3.opExtrude","SWEPT_FACE",FACE,{"disambiguationData":[OSD([subQ0])]})]}),makeQuery(id+"F3.boolean.opBoolean","COPY",FACE,{"derivedFrom":makeQuery(id+"F3.opExtrude","SWEPT_FACE",FACE,{"disambiguationData":[OSD([subQ1]),TDD([makeQuery(id+"F2.imprint","IMPRINT",EDGE,{"disambiguationData":[TD([[makeQuery(id+"F2.imprint","INTERSECT",VERTEX,{"derivedFrom":[subQ1,subQ0]}),-1.0]])],"derivedFrom":subQ1})])]})})],"blendedInto":[makeQuery(id+"F3.boolean.opBoolean","COPY",FACE,{"derivedFrom":makeQuery(id+"F3.opExtrude","SWEPT_FACE",FACE,{"disambiguationData":[OSD([subQ1]),TDD([makeQuery(id+"F2.imprint","IMPRINT",EDGE,{"disambiguationData":[TD([[makeQuery(id+"F2.imprint","INTERSECT",VERTEX,{"derivedFrom":[subQ1,subQ0]}),-1.0]])],"derivedFrom":subQ1})])]})})]});}
            var Q2;
            {var subQ0=sQuery(id+"F2.wireOp",EDGE,"E17.3.6.0");var subQ1=sQuery(id+"F2.wireOp",EDGE,"E12");Q2=makeQuery(id+"F6.opChamfer","BLEND_EDGE",EDGE,{"blendedFrom":[makeQuery(id+"F3.boolean.opBoolean","INTERSECT",EDGE,{"derivedFrom":[makeQuery(id+"F1.opRevolve","SWEPT_FACE",FACE,{"disambiguationData":[OSD([sQuery(id+"F0.wireOp",EDGE,"E9")])]}),makeQuery(id+"F3.opExtrude","SWEPT_FACE",FACE,{"disambiguationData":[OSD([subQ0])]})]}),makeQuery(id+"F3.boolean.opBoolean","COPY",FACE,{"derivedFrom":makeQuery(id+"F3.opExtrude","SWEPT_FACE",FACE,{"disambiguationData":[OSD([subQ1]),TDD([makeQuery(id+"F2.imprint","IMPRINT",EDGE,{"disambiguationData":[TD([[makeQuery(id+"F2.imprint","INTERSECT",VERTEX,{"derivedFrom":[subQ1,sQuery(id+"F2.wireOp",EDGE,"E17.6.6.0")]}),1.0]])],"derivedFrom":subQ1})])]})})],"blendedInto":[makeQuery(id+"F3.boolean.opBoolean","COPY",FACE,{"derivedFrom":makeQuery(id+"F3.opExtrude","SWEPT_FACE",FACE,{"disambiguationData":[OSD([subQ1]),TDD([makeQuery(id+"F2.imprint","IMPRINT",EDGE,{"disambiguationData":[TD([[makeQuery(id+"F2.imprint","INTERSECT",VERTEX,{"derivedFrom":[subQ1,sQuery(id+"F2.wireOp",EDGE,"E17.6.6.0")]}),1.0]])],"derivedFrom":subQ1})])]})})]});}
            var Q3;
            Q3=makeQuery(id+"F3.boolean.opBoolean","COPY",EDGE,{"derivedFrom":makeQuery(id+"F3.opExtrude","SWEPT_EDGE",EDGE,{"disambiguationData":[OSD([sQuery(id+"F2.wireOp",EDGE,"E12"),sQuery(id+"F2.wireOp",EDGE,"E17.3.6.0")])]})});
            var Q4;
            {var subQ0=sQuery(id+"F2.wireOp",EDGE,"E17.3.7.0");var subQ1=sQuery(id+"F2.wireOp",EDGE,"E12");Q4=makeQuery(id+"F6.opChamfer","BLEND_EDGE",EDGE,{"blendedFrom":[makeQuery(id+"F3.boolean.opBoolean","INTERSECT",EDGE,{"derivedFrom":[makeQuery(id+"F1.opRevolve","SWEPT_FACE",FACE,{"disambiguationData":[OSD([sQuery(id+"F0.wireOp",EDGE,"E9")])]}),makeQuery(id+"F3.opExtrude","SWEPT_FACE",FACE,{"disambiguationData":[OSD([subQ0])]})]}),makeQuery(id+"F3.boolean.opBoolean","COPY",FACE,{"derivedFrom":makeQuery(id+"F3.opExtrude","SWEPT_FACE",FACE,{"disambiguationData":[OSD([subQ1]),TDD([makeQuery(id+"F2.imprint","IMPRINT",EDGE,{"disambiguationData":[TD([[makeQuery(id+"F2.imprint","INTERSECT",VERTEX,{"derivedFrom":[subQ1,subQ0]}),-1.0]])],"derivedFrom":subQ1})])]})})],"blendedInto":[makeQuery(id+"F3.boolean.opBoolean","COPY",FACE,{"derivedFrom":makeQuery(id+"F3.opExtrude","SWEPT_FACE",FACE,{"disambiguationData":[OSD([subQ1]),TDD([makeQuery(id+"F2.imprint","IMPRINT",EDGE,{"disambiguationData":[TD([[makeQuery(id+"F2.imprint","INTERSECT",VERTEX,{"derivedFrom":[subQ1,subQ0]}),-1.0]])],"derivedFrom":subQ1})])]})})]});}
            var Q5;
            Q5=makeQuery(id+"F3.boolean.opBoolean","COPY",EDGE,{"derivedFrom":makeQuery(id+"F3.opExtrude","SWEPT_EDGE",EDGE,{"disambiguationData":[OSD([sQuery(id+"F2.wireOp",EDGE,"E12"),sQuery(id+"F2.wireOp",EDGE,"E17.3.7.0")])]})});
            var Q6;
            {var subQ0=sQuery(id+"F2.wireOp",EDGE,"E15");var subQ1=sQuery(id+"F2.wireOp",EDGE,"E12");Q6=makeQuery(id+"F6.opChamfer","BLEND_EDGE",EDGE,{"blendedFrom":[makeQuery(id+"F3.boolean.opBoolean","INTERSECT",EDGE,{"derivedFrom":[makeQuery(id+"F1.opRevolve","SWEPT_FACE",FACE,{"disambiguationData":[OSD([sQuery(id+"F0.wireOp",EDGE,"E9")])]}),makeQuery(id+"F3.opExtrude","SWEPT_FACE",FACE,{"disambiguationData":[OSD([subQ0])]})]}),makeQuery(id+"F3.boolean.opBoolean","COPY",FACE,{"derivedFrom":makeQuery(id+"F3.opExtrude","SWEPT_FACE",FACE,{"disambiguationData":[OSD([subQ1]),TDD([makeQuery(id+"F2.imprint","IMPRINT",EDGE,{"disambiguationData":[TD([[makeQuery(id+"F2.imprint","INTERSECT",VERTEX,{"derivedFrom":[subQ1,subQ0]}),-1.0]])],"derivedFrom":subQ1})])]})})],"blendedInto":[makeQuery(id+"F3.boolean.opBoolean","COPY",FACE,{"derivedFrom":makeQuery(id+"F3.opExtrude","SWEPT_FACE",FACE,{"disambiguationData":[OSD([subQ1]),TDD([makeQuery(id+"F2.imprint","IMPRINT",EDGE,{"disambiguationData":[TD([[makeQuery(id+"F2.imprint","INTERSECT",VERTEX,{"derivedFrom":[subQ1,subQ0]}),-1.0]])],"derivedFrom":subQ1})])]})})]});}
            var Q7;
            Q7=makeQuery(id+"F3.boolean.opBoolean","COPY",EDGE,{"derivedFrom":makeQuery(id+"F3.opExtrude","SWEPT_EDGE",EDGE,{"disambiguationData":[OSD([sQuery(id+"F2.wireOp",EDGE,"E12"),sQuery(id+"F2.wireOp",EDGE,"E15")])]})});
            var Q8;
            {var subQ0=sQuery(id+"F2.wireOp",EDGE,"E16.1.1");var subQ1=sQuery(id+"F2.wireOp",EDGE,"E12");Q8=makeQuery(id+"F6.opChamfer","BLEND_EDGE",EDGE,{"blendedFrom":[makeQuery(id+"F3.boolean.opBoolean","INTERSECT",EDGE,{"derivedFrom":[makeQuery(id+"F1.opRevolve","SWEPT_FACE",FACE,{"disambiguationData":[OSD([sQuery(id+"F0.wireOp",EDGE,"E9")])]}),makeQuery(id+"F3.opExtrude","SWEPT_FACE",FACE,{"disambiguationData":[OSD([subQ0])]})]}),makeQuery(id+"F3.boolean.opBoolean","COPY",FACE,{"derivedFrom":makeQuery(id+"F3.opExtrude","SWEPT_FACE",FACE,{"disambiguationData":[OSD([subQ1]),TDD([makeQuery(id+"F2.imprint","IMPRINT",EDGE,{"disambiguationData":[TD([[makeQuery(id+"F2.imprint","INTERSECT",VERTEX,{"derivedFrom":[subQ1,subQ0]}),-1.0]])],"derivedFrom":subQ1})])]})})],"blendedInto":[makeQuery(id+"F3.boolean.opBoolean","COPY",FACE,{"derivedFrom":makeQuery(id+"F3.opExtrude","SWEPT_FACE",FACE,{"disambiguationData":[OSD([subQ1]),TDD([makeQuery(id+"F2.imprint","IMPRINT",EDGE,{"disambiguationData":[TD([[makeQuery(id+"F2.imprint","INTERSECT",VERTEX,{"derivedFrom":[subQ1,subQ0]}),-1.0]])],"derivedFrom":subQ1})])]})})]});}
            var Q9;
            Q9=makeQuery(id+"F3.boolean.opBoolean","COPY",EDGE,{"derivedFrom":makeQuery(id+"F3.opExtrude","SWEPT_EDGE",EDGE,{"disambiguationData":[OSD([sQuery(id+"F2.wireOp",EDGE,"E12"),sQuery(id+"F2.wireOp",EDGE,"E16.1.1")])]})});
            var Q10;
            {var subQ0=sQuery(id+"F2.wireOp",EDGE,"E16.2.1");var subQ1=sQuery(id+"F2.wireOp",EDGE,"E12");Q10=makeQuery(id+"F6.opChamfer","BLEND_EDGE",EDGE,{"blendedFrom":[makeQuery(id+"F3.boolean.opBoolean","INTERSECT",EDGE,{"derivedFrom":[makeQuery(id+"F1.opRevolve","SWEPT_FACE",FACE,{"disambiguationData":[OSD([sQuery(id+"F0.wireOp",EDGE,"E9")])]}),makeQuery(id+"F3.opExtrude","SWEPT_FACE",FACE,{"disambiguationData":[OSD([subQ0])]})]}),makeQuery(id+"F3.boolean.opBoolean","COPY",FACE,{"derivedFrom":makeQuery(id+"F3.opExtrude","SWEPT_FACE",FACE,{"disambiguationData":[OSD([subQ1]),TDD([makeQuery(id+"F2.imprint","IMPRINT",EDGE,{"disambiguationData":[TD([[makeQuery(id+"F2.imprint","INTERSECT",VERTEX,{"derivedFrom":[subQ1,subQ0]}),-1.0]])],"derivedFrom":subQ1})])]})})],"blendedInto":[makeQuery(id+"F3.boolean.opBoolean","COPY",FACE,{"derivedFrom":makeQuery(id+"F3.opExtrude","SWEPT_FACE",FACE,{"disambiguationData":[OSD([subQ1]),TDD([makeQuery(id+"F2.imprint","IMPRINT",EDGE,{"disambiguationData":[TD([[makeQuery(id+"F2.imprint","INTERSECT",VERTEX,{"derivedFrom":[subQ1,subQ0]}),-1.0]])],"derivedFrom":subQ1})])]})})]});}
            var Q11;
            Q11=makeQuery(id+"F3.boolean.opBoolean","COPY",EDGE,{"derivedFrom":makeQuery(id+"F3.opExtrude","SWEPT_EDGE",EDGE,{"disambiguationData":[OSD([sQuery(id+"F2.wireOp",EDGE,"E12"),sQuery(id+"F2.wireOp",EDGE,"E16.2.1")])]})});
            var Q12;
            Q12=makeQuery(id+"F3.boolean.opBoolean","COPY",EDGE,{"derivedFrom":makeQuery(id+"F3.opExtrude","SWEPT_EDGE",EDGE,{"disambiguationData":[OSD([sQuery(id+"F2.wireOp",EDGE,"E12"),sQuery(id+"F2.wireOp",EDGE,"E17.3.3.0")])]})});
            var Q13;
            {var subQ0=sQuery(id+"F2.wireOp",EDGE,"E17.3.3.0");var subQ1=sQuery(id+"F2.wireOp",EDGE,"E12");Q13=makeQuery(id+"F6.opChamfer","BLEND_EDGE",EDGE,{"blendedFrom":[makeQuery(id+"F3.boolean.opBoolean","INTERSECT",EDGE,{"derivedFrom":[makeQuery(id+"F1.opRevolve","SWEPT_FACE",FACE,{"disambiguationData":[OSD([sQuery(id+"F0.wireOp",EDGE,"E9")])]}),makeQuery(id+"F3.opExtrude","SWEPT_FACE",FACE,{"disambiguationData":[OSD([subQ0])]})]}),makeQuery(id+"F3.boolean.opBoolean","COPY",FACE,{"derivedFrom":makeQuery(id+"F3.opExtrude","SWEPT_FACE",FACE,{"disambiguationData":[OSD([subQ1]),TDD([makeQuery(id+"F2.imprint","IMPRINT",EDGE,{"disambiguationData":[TD([[makeQuery(id+"F2.imprint","INTERSECT",VERTEX,{"derivedFrom":[subQ1,subQ0]}),-1.0]])],"derivedFrom":subQ1})])]})})],"blendedInto":[makeQuery(id+"F3.boolean.opBoolean","COPY",FACE,{"derivedFrom":makeQuery(id+"F3.opExtrude","SWEPT_FACE",FACE,{"disambiguationData":[OSD([subQ1]),TDD([makeQuery(id+"F2.imprint","IMPRINT",EDGE,{"disambiguationData":[TD([[makeQuery(id+"F2.imprint","INTERSECT",VERTEX,{"derivedFrom":[subQ1,subQ0]}),-1.0]])],"derivedFrom":subQ1})])]})})]});}
            var Q14;
            {var subQ0=sQuery(id+"F2.wireOp",EDGE,"E17.3.4.0");var subQ1=sQuery(id+"F2.wireOp",EDGE,"E12");Q14=makeQuery(id+"F6.opChamfer","BLEND_EDGE",EDGE,{"blendedFrom":[makeQuery(id+"F3.boolean.opBoolean","INTERSECT",EDGE,{"derivedFrom":[makeQuery(id+"F1.opRevolve","SWEPT_FACE",FACE,{"disambiguationData":[OSD([sQuery(id+"F0.wireOp",EDGE,"E9")])]}),makeQuery(id+"F3.opExtrude","SWEPT_FACE",FACE,{"disambiguationData":[OSD([subQ0])]})]}),makeQuery(id+"F3.boolean.opBoolean","COPY",FACE,{"derivedFrom":makeQuery(id+"F3.opExtrude","SWEPT_FACE",FACE,{"disambiguationData":[OSD([subQ1]),TDD([makeQuery(id+"F2.imprint","IMPRINT",EDGE,{"disambiguationData":[TD([[makeQuery(id+"F2.imprint","INTERSECT",VERTEX,{"derivedFrom":[subQ1,subQ0]}),-1.0]])],"derivedFrom":subQ1})])]})})],"blendedInto":[makeQuery(id+"F3.boolean.opBoolean","COPY",FACE,{"derivedFrom":makeQuery(id+"F3.opExtrude","SWEPT_FACE",FACE,{"disambiguationData":[OSD([subQ1]),TDD([makeQuery(id+"F2.imprint","IMPRINT",EDGE,{"disambiguationData":[TD([[makeQuery(id+"F2.imprint","INTERSECT",VERTEX,{"derivedFrom":[subQ1,subQ0]}),-1.0]])],"derivedFrom":subQ1})])]})})]});}
            var Q15;
            Q15=makeQuery(id+"F3.boolean.opBoolean","COPY",EDGE,{"derivedFrom":makeQuery(id+"F3.opExtrude","SWEPT_EDGE",EDGE,{"disambiguationData":[OSD([sQuery(id+"F2.wireOp",EDGE,"E12"),sQuery(id+"F2.wireOp",EDGE,"E17.3.4.0")])]})});
            fillet(context, id + "F9", {"entities" : qUnion([Q0, Q1, Q2, Q3, Q4, Q5, Q6, Q7, Q8, Q9, Q10, Q11, Q12, Q13, Q14, Q15]), "radius" : 1 * mm, "tangentPropagation" : true, "allowEdgeOverflow" : false});
        }
        {
            var Q0;
            {var subQ0=makeQuery(id+"F1.opRevolve","SWEPT_FACE",FACE,{"disambiguationData":[OSD([sQuery(id+"F0.wireOp",EDGE,"E10")])]});var subQ1=makeQuery(id+"F3.opExtrude","SWEPT_FACE",FACE,{"disambiguationData":[OSD([sQuery(id+"F2.wireOp",EDGE,"E16.1.1")])]});Q0=makeQuery(id+"F6.opChamfer","BLEND_EDGE",EDGE,{"blendedFrom":[makeQuery(id+"F3.boolean.opBoolean","INTERSECT",EDGE,{"derivedFrom":[subQ0,subQ1]}),makeQuery(id+"F3.boolean.opBoolean","SPLIT",FACE,{"disambiguationData":[TD([makeQuery(id+"F3.opExtrude","SWEPT_FACE",FACE,{"disambiguationData":[OSD([sQuery(id+"F2.wireOp",EDGE,"E13")])]})])],"derivedFrom":makeQuery(id+"F1.opRevolve","SWEPT_FACE",FACE,{"disambiguationData":[OSD([sQuery(id+"F0.wireOp",EDGE,"E3")])]})})],"blendedInto":[makeQuery(id+"F3.boolean.opBoolean","SPLIT",FACE,{"disambiguationData":[TD([makeQuery(id+"F3.opExtrude","SWEPT_FACE",FACE,{"disambiguationData":[OSD([sQuery(id+"F2.wireOp",EDGE,"E13")])]})])],"derivedFrom":makeQuery(id+"F1.opRevolve","SWEPT_FACE",FACE,{"disambiguationData":[OSD([sQuery(id+"F0.wireOp",EDGE,"E3")])]})})]});}
            var Q1;
            {var subQ0=makeQuery(id+"F1.opRevolve","SWEPT_FACE",FACE,{"disambiguationData":[OSD([sQuery(id+"F0.wireOp",EDGE,"E10")])]});var subQ1=makeQuery(id+"F3.opExtrude","SWEPT_FACE",FACE,{"disambiguationData":[OSD([sQuery(id+"F2.wireOp",EDGE,"E15")])]});Q1=makeQuery(id+"F6.opChamfer","BLEND_EDGE",EDGE,{"blendedFrom":[makeQuery(id+"F3.boolean.opBoolean","INTERSECT",EDGE,{"derivedFrom":[subQ0,subQ1]}),makeQuery(id+"F3.boolean.opBoolean","SPLIT",FACE,{"disambiguationData":[TD([subQ1])],"derivedFrom":makeQuery(id+"F1.opRevolve","SWEPT_FACE",FACE,{"disambiguationData":[OSD([sQuery(id+"F0.wireOp",EDGE,"E3")])]})})],"blendedInto":[makeQuery(id+"F3.boolean.opBoolean","SPLIT",FACE,{"disambiguationData":[TD([subQ1])],"derivedFrom":makeQuery(id+"F1.opRevolve","SWEPT_FACE",FACE,{"disambiguationData":[OSD([sQuery(id+"F0.wireOp",EDGE,"E3")])]})})]});}
            var Q2;
            {var subQ0=makeQuery(id+"F1.opRevolve","SWEPT_FACE",FACE,{"disambiguationData":[OSD([sQuery(id+"F0.wireOp",EDGE,"E10")])]});var subQ1=makeQuery(id+"F3.opExtrude","SWEPT_FACE",FACE,{"disambiguationData":[OSD([sQuery(id+"F2.wireOp",EDGE,"E17.3.7.0")])]});Q2=makeQuery(id+"F6.opChamfer","BLEND_EDGE",EDGE,{"blendedFrom":[makeQuery(id+"F3.boolean.opBoolean","INTERSECT",EDGE,{"derivedFrom":[subQ0,subQ1]}),makeQuery(id+"F3.boolean.opBoolean","SPLIT",FACE,{"disambiguationData":[TD([makeQuery(id+"F3.opExtrude","SWEPT_FACE",FACE,{"disambiguationData":[OSD([sQuery(id+"F2.wireOp",EDGE,"E17.6.6.0")])]})])],"derivedFrom":makeQuery(id+"F1.opRevolve","SWEPT_FACE",FACE,{"disambiguationData":[OSD([sQuery(id+"F0.wireOp",EDGE,"E3")])]})})],"blendedInto":[makeQuery(id+"F3.boolean.opBoolean","SPLIT",FACE,{"disambiguationData":[TD([makeQuery(id+"F3.opExtrude","SWEPT_FACE",FACE,{"disambiguationData":[OSD([sQuery(id+"F2.wireOp",EDGE,"E17.6.6.0")])]})])],"derivedFrom":makeQuery(id+"F1.opRevolve","SWEPT_FACE",FACE,{"disambiguationData":[OSD([sQuery(id+"F0.wireOp",EDGE,"E3")])]})})]});}
            var Q3;
            {var subQ0=makeQuery(id+"F1.opRevolve","SWEPT_FACE",FACE,{"disambiguationData":[OSD([sQuery(id+"F0.wireOp",EDGE,"E10")])]});var subQ1=makeQuery(id+"F3.opExtrude","SWEPT_FACE",FACE,{"disambiguationData":[OSD([sQuery(id+"F2.wireOp",EDGE,"E17.3.6.0")])]});Q3=makeQuery(id+"F6.opChamfer","BLEND_EDGE",EDGE,{"blendedFrom":[makeQuery(id+"F3.boolean.opBoolean","INTERSECT",EDGE,{"derivedFrom":[subQ0,subQ1]}),makeQuery(id+"F3.boolean.opBoolean","SPLIT",FACE,{"disambiguationData":[TD([makeQuery(id+"F3.opExtrude","SWEPT_FACE",FACE,{"disambiguationData":[OSD([sQuery(id+"F2.wireOp",EDGE,"E17.6.5.0")])]})])],"derivedFrom":makeQuery(id+"F1.opRevolve","SWEPT_FACE",FACE,{"disambiguationData":[OSD([sQuery(id+"F0.wireOp",EDGE,"E3")])]})})],"blendedInto":[makeQuery(id+"F3.boolean.opBoolean","SPLIT",FACE,{"disambiguationData":[TD([makeQuery(id+"F3.opExtrude","SWEPT_FACE",FACE,{"disambiguationData":[OSD([sQuery(id+"F2.wireOp",EDGE,"E17.6.5.0")])]})])],"derivedFrom":makeQuery(id+"F1.opRevolve","SWEPT_FACE",FACE,{"disambiguationData":[OSD([sQuery(id+"F0.wireOp",EDGE,"E3")])]})})]});}
            var Q4;
            {var subQ0=makeQuery(id+"F1.opRevolve","SWEPT_FACE",FACE,{"disambiguationData":[OSD([sQuery(id+"F0.wireOp",EDGE,"E10")])]});var subQ1=makeQuery(id+"F3.opExtrude","SWEPT_FACE",FACE,{"disambiguationData":[OSD([sQuery(id+"F2.wireOp",EDGE,"E16.2.1")])]});Q4=makeQuery(id+"F6.opChamfer","BLEND_EDGE",EDGE,{"blendedFrom":[makeQuery(id+"F3.boolean.opBoolean","INTERSECT",EDGE,{"derivedFrom":[subQ0,subQ1]}),makeQuery(id+"F3.boolean.opBoolean","SPLIT",FACE,{"disambiguationData":[TD([makeQuery(id+"F3.opExtrude","SWEPT_FACE",FACE,{"disambiguationData":[OSD([sQuery(id+"F2.wireOp",EDGE,"E16.1.2")])]})])],"derivedFrom":makeQuery(id+"F1.opRevolve","SWEPT_FACE",FACE,{"disambiguationData":[OSD([sQuery(id+"F0.wireOp",EDGE,"E3")])]})})],"blendedInto":[makeQuery(id+"F3.boolean.opBoolean","SPLIT",FACE,{"disambiguationData":[TD([makeQuery(id+"F3.opExtrude","SWEPT_FACE",FACE,{"disambiguationData":[OSD([sQuery(id+"F2.wireOp",EDGE,"E16.1.2")])]})])],"derivedFrom":makeQuery(id+"F1.opRevolve","SWEPT_FACE",FACE,{"disambiguationData":[OSD([sQuery(id+"F0.wireOp",EDGE,"E3")])]})})]});}
            var Q5;
            {var subQ0=makeQuery(id+"F1.opRevolve","SWEPT_FACE",FACE,{"disambiguationData":[OSD([sQuery(id+"F0.wireOp",EDGE,"E10")])]});var subQ1=makeQuery(id+"F3.opExtrude","SWEPT_FACE",FACE,{"disambiguationData":[OSD([sQuery(id+"F2.wireOp",EDGE,"E17.3.3.0")])]});Q5=makeQuery(id+"F6.opChamfer","BLEND_EDGE",EDGE,{"blendedFrom":[makeQuery(id+"F3.boolean.opBoolean","INTERSECT",EDGE,{"derivedFrom":[subQ0,subQ1]}),makeQuery(id+"F3.boolean.opBoolean","SPLIT",FACE,{"disambiguationData":[TD([makeQuery(id+"F3.opExtrude","SWEPT_FACE",FACE,{"disambiguationData":[OSD([sQuery(id+"F2.wireOp",EDGE,"E16.2.2")])]})])],"derivedFrom":makeQuery(id+"F1.opRevolve","SWEPT_FACE",FACE,{"disambiguationData":[OSD([sQuery(id+"F0.wireOp",EDGE,"E3")])]})})],"blendedInto":[makeQuery(id+"F3.boolean.opBoolean","SPLIT",FACE,{"disambiguationData":[TD([makeQuery(id+"F3.opExtrude","SWEPT_FACE",FACE,{"disambiguationData":[OSD([sQuery(id+"F2.wireOp",EDGE,"E16.2.2")])]})])],"derivedFrom":makeQuery(id+"F1.opRevolve","SWEPT_FACE",FACE,{"disambiguationData":[OSD([sQuery(id+"F0.wireOp",EDGE,"E3")])]})})]});}
            var Q6;
            {var subQ0=makeQuery(id+"F1.opRevolve","SWEPT_FACE",FACE,{"disambiguationData":[OSD([sQuery(id+"F0.wireOp",EDGE,"E10")])]});var subQ1=makeQuery(id+"F3.opExtrude","SWEPT_FACE",FACE,{"disambiguationData":[OSD([sQuery(id+"F2.wireOp",EDGE,"E17.3.4.0")])]});Q6=makeQuery(id+"F6.opChamfer","BLEND_EDGE",EDGE,{"blendedFrom":[makeQuery(id+"F3.boolean.opBoolean","INTERSECT",EDGE,{"derivedFrom":[subQ0,subQ1]}),makeQuery(id+"F3.boolean.opBoolean","SPLIT",FACE,{"disambiguationData":[TD([makeQuery(id+"F3.opExtrude","SWEPT_FACE",FACE,{"disambiguationData":[OSD([sQuery(id+"F2.wireOp",EDGE,"E17.6.3.0")])]})])],"derivedFrom":makeQuery(id+"F1.opRevolve","SWEPT_FACE",FACE,{"disambiguationData":[OSD([sQuery(id+"F0.wireOp",EDGE,"E3")])]})})],"blendedInto":[makeQuery(id+"F3.boolean.opBoolean","SPLIT",FACE,{"disambiguationData":[TD([makeQuery(id+"F3.opExtrude","SWEPT_FACE",FACE,{"disambiguationData":[OSD([sQuery(id+"F2.wireOp",EDGE,"E17.6.3.0")])]})])],"derivedFrom":makeQuery(id+"F1.opRevolve","SWEPT_FACE",FACE,{"disambiguationData":[OSD([sQuery(id+"F0.wireOp",EDGE,"E3")])]})})]});}
            var Q7;
            {var subQ0=makeQuery(id+"F1.opRevolve","SWEPT_FACE",FACE,{"disambiguationData":[OSD([sQuery(id+"F0.wireOp",EDGE,"E10")])]});var subQ1=makeQuery(id+"F3.opExtrude","SWEPT_FACE",FACE,{"disambiguationData":[OSD([sQuery(id+"F2.wireOp",EDGE,"E17.3.5.0")])]});Q7=makeQuery(id+"F6.opChamfer","BLEND_EDGE",EDGE,{"blendedFrom":[makeQuery(id+"F3.boolean.opBoolean","INTERSECT",EDGE,{"derivedFrom":[subQ0,subQ1]}),makeQuery(id+"F3.boolean.opBoolean","SPLIT",FACE,{"disambiguationData":[TD([makeQuery(id+"F3.opExtrude","SWEPT_FACE",FACE,{"disambiguationData":[OSD([sQuery(id+"F2.wireOp",EDGE,"E17.6.4.0")])]})])],"derivedFrom":makeQuery(id+"F1.opRevolve","SWEPT_FACE",FACE,{"disambiguationData":[OSD([sQuery(id+"F0.wireOp",EDGE,"E3")])]})})],"blendedInto":[makeQuery(id+"F3.boolean.opBoolean","SPLIT",FACE,{"disambiguationData":[TD([makeQuery(id+"F3.opExtrude","SWEPT_FACE",FACE,{"disambiguationData":[OSD([sQuery(id+"F2.wireOp",EDGE,"E17.6.4.0")])]})])],"derivedFrom":makeQuery(id+"F1.opRevolve","SWEPT_FACE",FACE,{"disambiguationData":[OSD([sQuery(id+"F0.wireOp",EDGE,"E3")])]})})]});}
            fillet(context, id + "F10", {"entities" : qUnion([Q0, Q1, Q2, Q3, Q4, Q5, Q6, Q7]), "radius" : 1 * mm, "allowEdgeOverflow" : false});
        }
        {
            var Q0;
            Q0=makeQuery(id+"F1.opRevolve","SWEPT_EDGE",EDGE,{"disambiguationData":[OSD([sQuery(id+"F0.wireOp",EDGE,"E4"),sQuery(id+"F0.wireOp",EDGE,"E9")])]});
            fillet(context, id + "F11", {"entities" : qUnion([Q0]), "radius" : 5 * mm, "tangentPropagation" : true, "allowEdgeOverflow" : false});
        }
        {
            var Q0;
            Q0=makeQuery(id+"F3.boolean.opBoolean","INTERSECT",EDGE,{"derivedFrom":[makeQuery(id+"F1.opRevolve","SWEPT_FACE",FACE,{"disambiguationData":[OSD([sQuery(id+"F0.wireOp",EDGE,"E9")])]}),makeQuery(id+"F3.opExtrude","SWEPT_FACE",FACE,{"disambiguationData":[OSD([sQuery(id+"F2.wireOp",EDGE,"E13")])]})]});
            var Q1;
            {var subQ0=makeQuery(id+"F1.opRevolve","SWEPT_FACE",FACE,{"disambiguationData":[OSD([sQuery(id+"F0.wireOp",EDGE,"E9")])]});Q1=makeQuery(id+"F6.opChamfer","BLEND_EDGE",EDGE,{"blendedFrom":[makeQuery(id+"F3.boolean.opBoolean","INTERSECT",EDGE,{"derivedFrom":[subQ0,makeQuery(id+"F3.opExtrude","SWEPT_FACE",FACE,{"disambiguationData":[OSD([sQuery(id+"F2.wireOp",EDGE,"E15")])]})]}),subQ0],"blendedInto":[subQ0]});}
            var Q2;
            {var subQ0=makeQuery(id+"F1.opRevolve","SWEPT_FACE",FACE,{"disambiguationData":[OSD([sQuery(id+"F0.wireOp",EDGE,"E11")])]});var subQ1=makeQuery(id+"F3.opExtrude","SWEPT_FACE",FACE,{"disambiguationData":[OSD([sQuery(id+"F2.wireOp",EDGE,"E15")])]});Q2=makeQuery(id+"F6.opChamfer","BLEND_EDGE",EDGE,{"blendedFrom":[makeQuery(id+"F3.boolean.opBoolean","INTERSECT",EDGE,{"derivedFrom":[subQ0,subQ1]}),makeQuery(id+"F3.boolean.opBoolean","SPLIT",FACE,{"disambiguationData":[TD([subQ1])],"derivedFrom":subQ0})],"blendedInto":[makeQuery(id+"F3.boolean.opBoolean","SPLIT",FACE,{"disambiguationData":[TD([subQ1])],"derivedFrom":subQ0})]});}
            var Q3;
            Q3=makeQuery(id+"F3.boolean.opBoolean","INTERSECT",EDGE,{"derivedFrom":[makeQuery(id+"F1.opRevolve","SWEPT_FACE",FACE,{"disambiguationData":[OSD([sQuery(id+"F0.wireOp",EDGE,"E11")])]}),makeQuery(id+"F3.opExtrude","SWEPT_FACE",FACE,{"disambiguationData":[OSD([sQuery(id+"F2.wireOp",EDGE,"E13")])]})]});
            var Q4;
            Q4=makeQuery(id+"F3.boolean.opBoolean","INTERSECT",EDGE,{"derivedFrom":[makeQuery(id+"F1.opRevolve","SWEPT_FACE",FACE,{"disambiguationData":[OSD([sQuery(id+"F0.wireOp",EDGE,"E10")])]}),makeQuery(id+"F3.opExtrude","SWEPT_FACE",FACE,{"disambiguationData":[OSD([sQuery(id+"F2.wireOp",EDGE,"E13")])]})]});
            var Q5;
            {var subQ0=makeQuery(id+"F1.opRevolve","SWEPT_FACE",FACE,{"disambiguationData":[OSD([sQuery(id+"F0.wireOp",EDGE,"E9")])]});Q5=makeQuery(id+"F6.opChamfer","BLEND_EDGE",EDGE,{"blendedFrom":[makeQuery(id+"F3.boolean.opBoolean","INTERSECT",EDGE,{"derivedFrom":[subQ0,makeQuery(id+"F3.opExtrude","SWEPT_FACE",FACE,{"disambiguationData":[OSD([sQuery(id+"F2.wireOp",EDGE,"E16.1.1")])]})]}),subQ0],"blendedInto":[subQ0]});}
            var Q6;
            {var subQ0=makeQuery(id+"F1.opRevolve","SWEPT_FACE",FACE,{"disambiguationData":[OSD([sQuery(id+"F0.wireOp",EDGE,"E10")])]});var subQ1=makeQuery(id+"F3.opExtrude","SWEPT_FACE",FACE,{"disambiguationData":[OSD([sQuery(id+"F2.wireOp",EDGE,"E15")])]});Q6=makeQuery(id+"F6.opChamfer","BLEND_EDGE",EDGE,{"blendedFrom":[makeQuery(id+"F3.boolean.opBoolean","INTERSECT",EDGE,{"derivedFrom":[subQ0,subQ1]}),makeQuery(id+"F3.boolean.opBoolean","SPLIT",FACE,{"disambiguationData":[TD([subQ1])],"derivedFrom":subQ0})],"blendedInto":[makeQuery(id+"F3.boolean.opBoolean","SPLIT",FACE,{"disambiguationData":[TD([subQ1])],"derivedFrom":subQ0})]});}
            var Q7;
            {var subQ0=sQuery(id+"F0.wireOp",EDGE,"E3");var subQ1=sQuery(id+"F0.wireOp",EDGE,"E10");Q7=makeQuery(id+"F3.boolean.opBoolean","SPLIT",EDGE,{"disambiguationData":[TD([makeQuery(id+"F3.opExtrude","SWEPT_FACE",FACE,{"disambiguationData":[OSD([sQuery(id+"F2.wireOp",EDGE,"E15")])]})])],"derivedFrom":makeQuery(id+"F1.opRevolve","SWEPT_EDGE",EDGE,{"disambiguationData":[OSD([subQ0,subQ1])]})});}
            var Q8;
            Q8=makeQuery(id+"F3.boolean.opBoolean","INTERSECT",EDGE,{"derivedFrom":[makeQuery(id+"F1.opRevolve","SWEPT_FACE",FACE,{"disambiguationData":[OSD([sQuery(id+"F0.wireOp",EDGE,"E9")])]}),makeQuery(id+"F3.opExtrude","SWEPT_FACE",FACE,{"disambiguationData":[OSD([sQuery(id+"F2.wireOp",EDGE,"E17.6.7.0")])]})]});
            var Q9;
            Q9=makeQuery(id+"F3.boolean.opBoolean","INTERSECT",EDGE,{"derivedFrom":[makeQuery(id+"F1.opRevolve","SWEPT_FACE",FACE,{"disambiguationData":[OSD([sQuery(id+"F0.wireOp",EDGE,"E10")])]}),makeQuery(id+"F3.opExtrude","SWEPT_FACE",FACE,{"disambiguationData":[OSD([sQuery(id+"F2.wireOp",EDGE,"E16.1.2")])]})]});
            var Q10;
            {var subQ0=makeQuery(id+"F1.opRevolve","SWEPT_FACE",FACE,{"disambiguationData":[OSD([sQuery(id+"F0.wireOp",EDGE,"E9")])]});Q10=makeQuery(id+"F6.opChamfer","BLEND_EDGE",EDGE,{"blendedFrom":[makeQuery(id+"F3.boolean.opBoolean","INTERSECT",EDGE,{"derivedFrom":[subQ0,makeQuery(id+"F3.opExtrude","SWEPT_FACE",FACE,{"disambiguationData":[OSD([sQuery(id+"F2.wireOp",EDGE,"E16.2.1")])]})]}),subQ0],"blendedInto":[subQ0]});}
            var Q11;
            Q11=makeQuery(id+"F3.boolean.opBoolean","INTERSECT",EDGE,{"derivedFrom":[makeQuery(id+"F1.opRevolve","SWEPT_FACE",FACE,{"disambiguationData":[OSD([sQuery(id+"F0.wireOp",EDGE,"E10")])]}),makeQuery(id+"F3.opExtrude","SWEPT_FACE",FACE,{"disambiguationData":[OSD([sQuery(id+"F2.wireOp",EDGE,"E16.2.2")])]})]});
            var Q12;
            Q12=makeQuery(id+"F3.boolean.opBoolean","INTERSECT",EDGE,{"derivedFrom":[makeQuery(id+"F1.opRevolve","SWEPT_FACE",FACE,{"disambiguationData":[OSD([sQuery(id+"F0.wireOp",EDGE,"E10")])]}),makeQuery(id+"F3.opExtrude","SWEPT_FACE",FACE,{"disambiguationData":[OSD([sQuery(id+"F2.wireOp",EDGE,"E17.6.3.0")])]})]});
            var Q13;
            Q13=makeQuery(id+"F3.boolean.opBoolean","INTERSECT",EDGE,{"derivedFrom":[makeQuery(id+"F1.opRevolve","SWEPT_FACE",FACE,{"disambiguationData":[OSD([sQuery(id+"F0.wireOp",EDGE,"E9")])]}),makeQuery(id+"F3.opExtrude","SWEPT_FACE",FACE,{"disambiguationData":[OSD([sQuery(id+"F2.wireOp",EDGE,"E17.6.3.0")])]})]});
            var Q14;
            {var subQ0=makeQuery(id+"F1.opRevolve","SWEPT_FACE",FACE,{"disambiguationData":[OSD([sQuery(id+"F0.wireOp",EDGE,"E9")])]});Q14=makeQuery(id+"F6.opChamfer","BLEND_EDGE",EDGE,{"blendedFrom":[makeQuery(id+"F3.boolean.opBoolean","INTERSECT",EDGE,{"derivedFrom":[subQ0,makeQuery(id+"F3.opExtrude","SWEPT_FACE",FACE,{"disambiguationData":[OSD([sQuery(id+"F2.wireOp",EDGE,"E17.3.3.0")])]})]}),subQ0],"blendedInto":[subQ0]});}
            var Q15;
            {var subQ0=sQuery(id+"F2.wireOp",EDGE,"E12");Q15=makeQuery(id+"F11.opFillet","BLEND_EDGE",EDGE,{"blendedFrom":[makeQuery(id+"F1.opRevolve","SWEPT_EDGE",EDGE,{"disambiguationData":[OSD([sQuery(id+"F0.wireOp",EDGE,"E4"),sQuery(id+"F0.wireOp",EDGE,"E9")])]}),makeQuery(id+"F3.boolean.opBoolean","COPY",FACE,{"derivedFrom":makeQuery(id+"F3.opExtrude","SWEPT_FACE",FACE,{"disambiguationData":[OSD([subQ0]),TDD([makeQuery(id+"F2.imprint","IMPRINT",EDGE,{"disambiguationData":[TD([[makeQuery(id+"F2.imprint","INTERSECT",VERTEX,{"derivedFrom":[subQ0,sQuery(id+"F2.wireOp",EDGE,"E17.3.3.0")]}),-1.0]])],"derivedFrom":subQ0})])]})})],"blendedInto":[makeQuery(id+"F3.boolean.opBoolean","COPY",FACE,{"derivedFrom":makeQuery(id+"F3.opExtrude","SWEPT_FACE",FACE,{"disambiguationData":[OSD([subQ0]),TDD([makeQuery(id+"F2.imprint","IMPRINT",EDGE,{"disambiguationData":[TD([[makeQuery(id+"F2.imprint","INTERSECT",VERTEX,{"derivedFrom":[subQ0,sQuery(id+"F2.wireOp",EDGE,"E17.3.3.0")]}),-1.0]])],"derivedFrom":subQ0})])]})})]});}
            var Q16;
            {var subQ0=sQuery(id+"F2.wireOp",EDGE,"E12");Q16=makeQuery(id+"F11.opFillet","BLEND_EDGE",EDGE,{"blendedFrom":[makeQuery(id+"F1.opRevolve","SWEPT_EDGE",EDGE,{"disambiguationData":[OSD([sQuery(id+"F0.wireOp",EDGE,"E4"),sQuery(id+"F0.wireOp",EDGE,"E9")])]}),makeQuery(id+"F3.boolean.opBoolean","COPY",FACE,{"derivedFrom":makeQuery(id+"F3.opExtrude","SWEPT_FACE",FACE,{"disambiguationData":[OSD([subQ0]),TDD([makeQuery(id+"F2.imprint","IMPRINT",EDGE,{"disambiguationData":[TD([[makeQuery(id+"F2.imprint","INTERSECT",VERTEX,{"derivedFrom":[subQ0,sQuery(id+"F2.wireOp",EDGE,"E17.3.4.0")]}),-1.0]])],"derivedFrom":subQ0})])]})})],"blendedInto":[makeQuery(id+"F3.boolean.opBoolean","COPY",FACE,{"derivedFrom":makeQuery(id+"F3.opExtrude","SWEPT_FACE",FACE,{"disambiguationData":[OSD([subQ0]),TDD([makeQuery(id+"F2.imprint","IMPRINT",EDGE,{"disambiguationData":[TD([[makeQuery(id+"F2.imprint","INTERSECT",VERTEX,{"derivedFrom":[subQ0,sQuery(id+"F2.wireOp",EDGE,"E17.3.4.0")]}),-1.0]])],"derivedFrom":subQ0})])]})})]});}
            var Q17;
            Q17=makeQuery(id+"F3.boolean.opBoolean","INTERSECT",EDGE,{"derivedFrom":[makeQuery(id+"F1.opRevolve","SWEPT_FACE",FACE,{"disambiguationData":[OSD([sQuery(id+"F0.wireOp",EDGE,"E9")])]}),makeQuery(id+"F3.opExtrude","SWEPT_FACE",FACE,{"disambiguationData":[OSD([sQuery(id+"F2.wireOp",EDGE,"E17.6.4.0")])]})]});
            var Q18;
            {var subQ0=makeQuery(id+"F1.opRevolve","SWEPT_FACE",FACE,{"disambiguationData":[OSD([sQuery(id+"F0.wireOp",EDGE,"E9")])]});Q18=makeQuery(id+"F6.opChamfer","BLEND_EDGE",EDGE,{"blendedFrom":[makeQuery(id+"F3.boolean.opBoolean","INTERSECT",EDGE,{"derivedFrom":[subQ0,makeQuery(id+"F3.opExtrude","SWEPT_FACE",FACE,{"disambiguationData":[OSD([sQuery(id+"F2.wireOp",EDGE,"E17.3.4.0")])]})]}),subQ0],"blendedInto":[subQ0]});}
            var Q19;
            Q19=makeQuery(id+"F3.boolean.opBoolean","INTERSECT",EDGE,{"derivedFrom":[makeQuery(id+"F1.opRevolve","SWEPT_FACE",FACE,{"disambiguationData":[OSD([sQuery(id+"F0.wireOp",EDGE,"E9")])]}),makeQuery(id+"F3.opExtrude","SWEPT_FACE",FACE,{"disambiguationData":[OSD([sQuery(id+"F2.wireOp",EDGE,"E17.6.5.0")])]})]});
            var Q20;
            Q20=makeQuery(id+"F3.boolean.opBoolean","INTERSECT",EDGE,{"derivedFrom":[makeQuery(id+"F1.opRevolve","SWEPT_FACE",FACE,{"disambiguationData":[OSD([sQuery(id+"F0.wireOp",EDGE,"E9")])]}),makeQuery(id+"F3.opExtrude","SWEPT_FACE",FACE,{"disambiguationData":[OSD([sQuery(id+"F2.wireOp",EDGE,"E17.6.6.0")])]})]});
            var Q21;
            {var subQ0=sQuery(id+"F2.wireOp",EDGE,"E12");Q21=makeQuery(id+"F11.opFillet","BLEND_EDGE",EDGE,{"blendedFrom":[makeQuery(id+"F1.opRevolve","SWEPT_EDGE",EDGE,{"disambiguationData":[OSD([sQuery(id+"F0.wireOp",EDGE,"E4"),sQuery(id+"F0.wireOp",EDGE,"E9")])]}),makeQuery(id+"F3.boolean.opBoolean","COPY",FACE,{"derivedFrom":makeQuery(id+"F3.opExtrude","SWEPT_FACE",FACE,{"disambiguationData":[OSD([subQ0]),TDD([makeQuery(id+"F2.imprint","IMPRINT",EDGE,{"disambiguationData":[TD([[makeQuery(id+"F2.imprint","INTERSECT",VERTEX,{"derivedFrom":[subQ0,sQuery(id+"F2.wireOp",EDGE,"E17.3.5.0")]}),-1.0]])],"derivedFrom":subQ0})])]})})],"blendedInto":[makeQuery(id+"F3.boolean.opBoolean","COPY",FACE,{"derivedFrom":makeQuery(id+"F3.opExtrude","SWEPT_FACE",FACE,{"disambiguationData":[OSD([subQ0]),TDD([makeQuery(id+"F2.imprint","IMPRINT",EDGE,{"disambiguationData":[TD([[makeQuery(id+"F2.imprint","INTERSECT",VERTEX,{"derivedFrom":[subQ0,sQuery(id+"F2.wireOp",EDGE,"E17.3.5.0")]}),-1.0]])],"derivedFrom":subQ0})])]})})]});}
            var Q22;
            {var subQ0=makeQuery(id+"F1.opRevolve","SWEPT_FACE",FACE,{"disambiguationData":[OSD([sQuery(id+"F0.wireOp",EDGE,"E9")])]});Q22=makeQuery(id+"F6.opChamfer","BLEND_EDGE",EDGE,{"blendedFrom":[makeQuery(id+"F3.boolean.opBoolean","INTERSECT",EDGE,{"derivedFrom":[subQ0,makeQuery(id+"F3.opExtrude","SWEPT_FACE",FACE,{"disambiguationData":[OSD([sQuery(id+"F2.wireOp",EDGE,"E17.3.5.0")])]})]}),subQ0],"blendedInto":[subQ0]});}
            var Q23;
            {var subQ0=makeQuery(id+"F1.opRevolve","SWEPT_FACE",FACE,{"disambiguationData":[OSD([sQuery(id+"F0.wireOp",EDGE,"E9")])]});Q23=makeQuery(id+"F6.opChamfer","BLEND_EDGE",EDGE,{"blendedFrom":[makeQuery(id+"F3.boolean.opBoolean","INTERSECT",EDGE,{"derivedFrom":[subQ0,makeQuery(id+"F3.opExtrude","SWEPT_FACE",FACE,{"disambiguationData":[OSD([sQuery(id+"F2.wireOp",EDGE,"E17.3.6.0")])]})]}),subQ0],"blendedInto":[subQ0]});}
            var Q24;
            {var subQ0=sQuery(id+"F2.wireOp",EDGE,"E12");Q24=makeQuery(id+"F11.opFillet","BLEND_EDGE",EDGE,{"blendedFrom":[makeQuery(id+"F1.opRevolve","SWEPT_EDGE",EDGE,{"disambiguationData":[OSD([sQuery(id+"F0.wireOp",EDGE,"E4"),sQuery(id+"F0.wireOp",EDGE,"E9")])]}),makeQuery(id+"F3.boolean.opBoolean","COPY",FACE,{"derivedFrom":makeQuery(id+"F3.opExtrude","SWEPT_FACE",FACE,{"disambiguationData":[OSD([subQ0]),TDD([makeQuery(id+"F2.imprint","IMPRINT",EDGE,{"disambiguationData":[TD([[makeQuery(id+"F2.imprint","INTERSECT",VERTEX,{"derivedFrom":[subQ0,sQuery(id+"F2.wireOp",EDGE,"E17.6.6.0")]}),1.0]])],"derivedFrom":subQ0})])]})})],"blendedInto":[makeQuery(id+"F3.boolean.opBoolean","COPY",FACE,{"derivedFrom":makeQuery(id+"F3.opExtrude","SWEPT_FACE",FACE,{"disambiguationData":[OSD([subQ0]),TDD([makeQuery(id+"F2.imprint","IMPRINT",EDGE,{"disambiguationData":[TD([[makeQuery(id+"F2.imprint","INTERSECT",VERTEX,{"derivedFrom":[subQ0,sQuery(id+"F2.wireOp",EDGE,"E17.6.6.0")]}),1.0]])],"derivedFrom":subQ0})])]})})]});}
            var Q25;
            Q25=makeQuery(id+"F3.boolean.opBoolean","INTERSECT",EDGE,{"derivedFrom":[makeQuery(id+"F1.opRevolve","SWEPT_FACE",FACE,{"disambiguationData":[OSD([sQuery(id+"F0.wireOp",EDGE,"E10")])]}),makeQuery(id+"F3.opExtrude","SWEPT_FACE",FACE,{"disambiguationData":[OSD([sQuery(id+"F2.wireOp",EDGE,"E17.6.4.0")])]})]});
            var Q26;
            {var subQ0=makeQuery(id+"F1.opRevolve","SWEPT_FACE",FACE,{"disambiguationData":[OSD([sQuery(id+"F0.wireOp",EDGE,"E10")])]});var subQ1=makeQuery(id+"F3.opExtrude","SWEPT_FACE",FACE,{"disambiguationData":[OSD([sQuery(id+"F2.wireOp",EDGE,"E17.3.5.0")])]});Q26=makeQuery(id+"F6.opChamfer","BLEND_EDGE",EDGE,{"blendedFrom":[makeQuery(id+"F3.boolean.opBoolean","INTERSECT",EDGE,{"derivedFrom":[subQ0,subQ1]}),makeQuery(id+"F3.boolean.opBoolean","SPLIT",FACE,{"disambiguationData":[TD([makeQuery(id+"F3.opExtrude","SWEPT_FACE",FACE,{"disambiguationData":[OSD([sQuery(id+"F2.wireOp",EDGE,"E17.6.4.0")])]})])],"derivedFrom":subQ0})],"blendedInto":[makeQuery(id+"F3.boolean.opBoolean","SPLIT",FACE,{"disambiguationData":[TD([makeQuery(id+"F3.opExtrude","SWEPT_FACE",FACE,{"disambiguationData":[OSD([sQuery(id+"F2.wireOp",EDGE,"E17.6.4.0")])]})])],"derivedFrom":subQ0})]});}
            var Q27;
            {var subQ0=sQuery(id+"F0.wireOp",EDGE,"E3");var subQ1=sQuery(id+"F0.wireOp",EDGE,"E10");Q27=makeQuery(id+"F3.boolean.opBoolean","SPLIT",EDGE,{"disambiguationData":[TD([makeQuery(id+"F3.opExtrude","SWEPT_FACE",FACE,{"disambiguationData":[OSD([sQuery(id+"F2.wireOp",EDGE,"E17.6.4.0")])]})])],"derivedFrom":makeQuery(id+"F1.opRevolve","SWEPT_EDGE",EDGE,{"disambiguationData":[OSD([subQ0,subQ1])]})});}
            var Q28;
            Q28=makeQuery(id+"F3.boolean.opBoolean","INTERSECT",EDGE,{"derivedFrom":[makeQuery(id+"F1.opRevolve","SWEPT_FACE",FACE,{"disambiguationData":[OSD([sQuery(id+"F0.wireOp",EDGE,"E11")])]}),makeQuery(id+"F3.opExtrude","SWEPT_FACE",FACE,{"disambiguationData":[OSD([sQuery(id+"F2.wireOp",EDGE,"E17.6.4.0")])]})]});
            var Q29;
            {var subQ0=makeQuery(id+"F1.opRevolve","SWEPT_FACE",FACE,{"disambiguationData":[OSD([sQuery(id+"F0.wireOp",EDGE,"E11")])]});var subQ1=makeQuery(id+"F3.opExtrude","SWEPT_FACE",FACE,{"disambiguationData":[OSD([sQuery(id+"F2.wireOp",EDGE,"E17.3.5.0")])]});Q29=makeQuery(id+"F6.opChamfer","BLEND_EDGE",EDGE,{"blendedFrom":[makeQuery(id+"F3.boolean.opBoolean","INTERSECT",EDGE,{"derivedFrom":[subQ0,subQ1]}),makeQuery(id+"F3.boolean.opBoolean","SPLIT",FACE,{"disambiguationData":[TD([makeQuery(id+"F3.opExtrude","SWEPT_FACE",FACE,{"disambiguationData":[OSD([sQuery(id+"F2.wireOp",EDGE,"E17.6.4.0")])]})])],"derivedFrom":subQ0})],"blendedInto":[makeQuery(id+"F3.boolean.opBoolean","SPLIT",FACE,{"disambiguationData":[TD([makeQuery(id+"F3.opExtrude","SWEPT_FACE",FACE,{"disambiguationData":[OSD([sQuery(id+"F2.wireOp",EDGE,"E17.6.4.0")])]})])],"derivedFrom":subQ0})]});}
            var Q30;
            Q30=makeQuery(id+"F3.boolean.opBoolean","INTERSECT",EDGE,{"derivedFrom":[makeQuery(id+"F1.opRevolve","SWEPT_FACE",FACE,{"disambiguationData":[OSD([sQuery(id+"F0.wireOp",EDGE,"E10")])]}),makeQuery(id+"F3.opExtrude","SWEPT_FACE",FACE,{"disambiguationData":[OSD([sQuery(id+"F2.wireOp",EDGE,"E17.6.5.0")])]})]});
            var Q31;
            {var subQ0=makeQuery(id+"F1.opRevolve","SWEPT_FACE",FACE,{"disambiguationData":[OSD([sQuery(id+"F0.wireOp",EDGE,"E10")])]});var subQ1=makeQuery(id+"F3.opExtrude","SWEPT_FACE",FACE,{"disambiguationData":[OSD([sQuery(id+"F2.wireOp",EDGE,"E17.3.6.0")])]});Q31=makeQuery(id+"F6.opChamfer","BLEND_EDGE",EDGE,{"blendedFrom":[makeQuery(id+"F3.boolean.opBoolean","INTERSECT",EDGE,{"derivedFrom":[subQ0,subQ1]}),makeQuery(id+"F3.boolean.opBoolean","SPLIT",FACE,{"disambiguationData":[TD([makeQuery(id+"F3.opExtrude","SWEPT_FACE",FACE,{"disambiguationData":[OSD([sQuery(id+"F2.wireOp",EDGE,"E17.6.5.0")])]})])],"derivedFrom":subQ0})],"blendedInto":[makeQuery(id+"F3.boolean.opBoolean","SPLIT",FACE,{"disambiguationData":[TD([makeQuery(id+"F3.opExtrude","SWEPT_FACE",FACE,{"disambiguationData":[OSD([sQuery(id+"F2.wireOp",EDGE,"E17.6.5.0")])]})])],"derivedFrom":subQ0})]});}
            var Q32;
            Q32=makeQuery(id+"F3.boolean.opBoolean","INTERSECT",EDGE,{"derivedFrom":[makeQuery(id+"F1.opRevolve","SWEPT_FACE",FACE,{"disambiguationData":[OSD([sQuery(id+"F0.wireOp",EDGE,"E10")])]}),makeQuery(id+"F3.opExtrude","SWEPT_FACE",FACE,{"disambiguationData":[OSD([sQuery(id+"F2.wireOp",EDGE,"E17.6.6.0")])]})]});
            var Q33;
            {var subQ0=makeQuery(id+"F1.opRevolve","SWEPT_FACE",FACE,{"disambiguationData":[OSD([sQuery(id+"F0.wireOp",EDGE,"E10")])]});var subQ1=makeQuery(id+"F3.opExtrude","SWEPT_FACE",FACE,{"disambiguationData":[OSD([sQuery(id+"F2.wireOp",EDGE,"E17.3.7.0")])]});Q33=makeQuery(id+"F6.opChamfer","BLEND_EDGE",EDGE,{"blendedFrom":[makeQuery(id+"F3.boolean.opBoolean","INTERSECT",EDGE,{"derivedFrom":[subQ0,subQ1]}),makeQuery(id+"F3.boolean.opBoolean","SPLIT",FACE,{"disambiguationData":[TD([makeQuery(id+"F3.opExtrude","SWEPT_FACE",FACE,{"disambiguationData":[OSD([sQuery(id+"F2.wireOp",EDGE,"E17.6.6.0")])]})])],"derivedFrom":subQ0})],"blendedInto":[makeQuery(id+"F3.boolean.opBoolean","SPLIT",FACE,{"disambiguationData":[TD([makeQuery(id+"F3.opExtrude","SWEPT_FACE",FACE,{"disambiguationData":[OSD([sQuery(id+"F2.wireOp",EDGE,"E17.6.6.0")])]})])],"derivedFrom":subQ0})]});}
            var Q34;
            {var subQ0=sQuery(id+"F0.wireOp",EDGE,"E3");var subQ1=sQuery(id+"F0.wireOp",EDGE,"E10");Q34=makeQuery(id+"F3.boolean.opBoolean","SPLIT",EDGE,{"disambiguationData":[TD([makeQuery(id+"F3.opExtrude","SWEPT_FACE",FACE,{"disambiguationData":[OSD([sQuery(id+"F2.wireOp",EDGE,"E17.6.6.0")])]})])],"derivedFrom":makeQuery(id+"F1.opRevolve","SWEPT_EDGE",EDGE,{"disambiguationData":[OSD([subQ0,subQ1])]})});}
            var Q35;
            {var subQ0=makeQuery(id+"F1.opRevolve","SWEPT_FACE",FACE,{"disambiguationData":[OSD([sQuery(id+"F0.wireOp",EDGE,"E11")])]});var subQ1=makeQuery(id+"F3.opExtrude","SWEPT_FACE",FACE,{"disambiguationData":[OSD([sQuery(id+"F2.wireOp",EDGE,"E17.3.7.0")])]});Q35=makeQuery(id+"F6.opChamfer","BLEND_EDGE",EDGE,{"blendedFrom":[makeQuery(id+"F3.boolean.opBoolean","INTERSECT",EDGE,{"derivedFrom":[subQ0,subQ1]}),makeQuery(id+"F3.boolean.opBoolean","SPLIT",FACE,{"disambiguationData":[TD([makeQuery(id+"F3.opExtrude","SWEPT_FACE",FACE,{"disambiguationData":[OSD([sQuery(id+"F2.wireOp",EDGE,"E17.6.6.0")])]})])],"derivedFrom":subQ0})],"blendedInto":[makeQuery(id+"F3.boolean.opBoolean","SPLIT",FACE,{"disambiguationData":[TD([makeQuery(id+"F3.opExtrude","SWEPT_FACE",FACE,{"disambiguationData":[OSD([sQuery(id+"F2.wireOp",EDGE,"E17.6.6.0")])]})])],"derivedFrom":subQ0})]});}
            var Q36;
            Q36=makeQuery(id+"F3.boolean.opBoolean","INTERSECT",EDGE,{"derivedFrom":[makeQuery(id+"F1.opRevolve","SWEPT_FACE",FACE,{"disambiguationData":[OSD([sQuery(id+"F0.wireOp",EDGE,"E11")])]}),makeQuery(id+"F3.opExtrude","SWEPT_FACE",FACE,{"disambiguationData":[OSD([sQuery(id+"F2.wireOp",EDGE,"E17.6.6.0")])]})]});
            chamfer(context, id + "F12", {"entities" : qUnion([Q0, Q1, Q2, Q3, Q4, Q5, Q6, Q7, Q8, Q9, Q10, Q11, Q12, Q13, Q14, Q15, Q16, Q17, Q18, Q19, Q20, Q21, Q22, Q23, Q24, Q25, Q26, Q27, Q28, Q29, Q30, Q31, Q32, Q33, Q34, Q35, Q36]), "width" : 1 * mm, "tangentPropagation" : true});
        }
        {
            var Q0;
            Q0=makeQuery(id+"F3.boolean.opBoolean","INTERSECT",EDGE,{"derivedFrom":[makeQuery(id+"F1.opRevolve","SWEPT_FACE",FACE,{"disambiguationData":[OSD([sQuery(id+"F0.wireOp",EDGE,"E8")])]}),makeQuery(id+"F3.opExtrude","SWEPT_FACE",FACE,{"disambiguationData":[OSD([sQuery(id+"F2.wireOp",EDGE,"E16.1.1")])]})]});
            var Q1;
            Q1=makeQuery(id+"F3.boolean.opBoolean","INTERSECT",EDGE,{"derivedFrom":[makeQuery(id+"F1.opRevolve","SWEPT_FACE",FACE,{"disambiguationData":[OSD([sQuery(id+"F0.wireOp",EDGE,"E8")])]}),makeQuery(id+"F3.opExtrude","SWEPT_FACE",FACE,{"disambiguationData":[OSD([sQuery(id+"F2.wireOp",EDGE,"E15")])]})]});
            var Q2;
            Q2=makeQuery(id+"F3.boolean.opBoolean","INTERSECT",EDGE,{"derivedFrom":[makeQuery(id+"F1.opRevolve","SWEPT_FACE",FACE,{"disambiguationData":[OSD([sQuery(id+"F0.wireOp",EDGE,"E8")])]}),makeQuery(id+"F3.opExtrude","SWEPT_FACE",FACE,{"disambiguationData":[OSD([sQuery(id+"F2.wireOp",EDGE,"E17.3.7.0")])]})]});
            var Q3;
            Q3=makeQuery(id+"F3.boolean.opBoolean","INTERSECT",EDGE,{"derivedFrom":[makeQuery(id+"F1.opRevolve","SWEPT_FACE",FACE,{"disambiguationData":[OSD([sQuery(id+"F0.wireOp",EDGE,"E8")])]}),makeQuery(id+"F3.opExtrude","SWEPT_FACE",FACE,{"disambiguationData":[OSD([sQuery(id+"F2.wireOp",EDGE,"E17.3.6.0")])]})]});
            var Q4;
            Q4=makeQuery(id+"F3.boolean.opBoolean","INTERSECT",EDGE,{"derivedFrom":[makeQuery(id+"F1.opRevolve","SWEPT_FACE",FACE,{"disambiguationData":[OSD([sQuery(id+"F0.wireOp",EDGE,"E8")])]}),makeQuery(id+"F3.opExtrude","SWEPT_FACE",FACE,{"disambiguationData":[OSD([sQuery(id+"F2.wireOp",EDGE,"E17.3.5.0")])]})]});
            var Q5;
            Q5=makeQuery(id+"F3.boolean.opBoolean","INTERSECT",EDGE,{"derivedFrom":[makeQuery(id+"F1.opRevolve","SWEPT_FACE",FACE,{"disambiguationData":[OSD([sQuery(id+"F0.wireOp",EDGE,"E8")])]}),makeQuery(id+"F3.opExtrude","SWEPT_FACE",FACE,{"disambiguationData":[OSD([sQuery(id+"F2.wireOp",EDGE,"E17.3.4.0")])]})]});
            var Q6;
            Q6=makeQuery(id+"F3.boolean.opBoolean","INTERSECT",EDGE,{"derivedFrom":[makeQuery(id+"F1.opRevolve","SWEPT_FACE",FACE,{"disambiguationData":[OSD([sQuery(id+"F0.wireOp",EDGE,"E8")])]}),makeQuery(id+"F3.opExtrude","SWEPT_FACE",FACE,{"disambiguationData":[OSD([sQuery(id+"F2.wireOp",EDGE,"E17.3.3.0")])]})]});
            var Q7;
            Q7=makeQuery(id+"F3.boolean.opBoolean","INTERSECT",EDGE,{"derivedFrom":[makeQuery(id+"F1.opRevolve","SWEPT_FACE",FACE,{"disambiguationData":[OSD([sQuery(id+"F0.wireOp",EDGE,"E8")])]}),makeQuery(id+"F3.opExtrude","SWEPT_FACE",FACE,{"disambiguationData":[OSD([sQuery(id+"F2.wireOp",EDGE,"E16.2.1")])]})]});
            var Q8;
            {var subQ0=sQuery(id+"F0.wireOp",EDGE,"E3");var subQ1=sQuery(id+"F0.wireOp",EDGE,"E6");Q8=makeQuery(id+"F3.boolean.opBoolean","SPLIT",EDGE,{"disambiguationData":[TD([makeQuery(id+"F3.opExtrude","SWEPT_FACE",FACE,{"disambiguationData":[OSD([sQuery(id+"F2.wireOp",EDGE,"E13")])]})])],"derivedFrom":makeQuery(id+"F1.opRevolve","SWEPT_EDGE",EDGE,{"disambiguationData":[OSD([subQ0,subQ1])]})});}
            var Q9;
            Q9=makeQuery(id+"F3.boolean.opBoolean","INTERSECT",EDGE,{"derivedFrom":[makeQuery(id+"F1.opRevolve","SWEPT_FACE",FACE,{"disambiguationData":[OSD([sQuery(id+"F0.wireOp",EDGE,"E6")])]}),makeQuery(id+"F3.opExtrude","SWEPT_FACE",FACE,{"disambiguationData":[OSD([sQuery(id+"F2.wireOp",EDGE,"E16.1.1")])]})]});
            var Q10;
            {var subQ0=makeQuery(id+"F1.opRevolve","SWEPT_FACE",FACE,{"disambiguationData":[OSD([sQuery(id+"F0.wireOp",EDGE,"E10")])]});var subQ1=makeQuery(id+"F3.opExtrude","SWEPT_FACE",FACE,{"disambiguationData":[OSD([sQuery(id+"F2.wireOp",EDGE,"E16.1.1")])]});var subQ2=makeQuery(id+"F1.opRevolve","SWEPT_FACE",FACE,{"disambiguationData":[OSD([sQuery(id+"F0.wireOp",EDGE,"E3")])]});var subQ3=makeQuery(id+"F3.opExtrude","SWEPT_FACE",FACE,{"disambiguationData":[OSD([sQuery(id+"F2.wireOp",EDGE,"E13")])]});var subQ4=makeQuery(id+"F1.opRevolve","SWEPT_FACE",FACE,{"disambiguationData":[OSD([sQuery(id+"F0.wireOp",EDGE,"E6")])]});Q10=makeQuery(id+"F10.opFillet","BLEND_EDGE",EDGE,{"blendedFrom":[makeQuery(id+"F6.opChamfer","BLEND_EDGE",EDGE,{"blendedFrom":[makeQuery(id+"F3.boolean.opBoolean","INTERSECT",EDGE,{"derivedFrom":[subQ0,subQ1]}),makeQuery(id+"F3.boolean.opBoolean","SPLIT",FACE,{"disambiguationData":[TD([subQ3])],"derivedFrom":subQ2})],"blendedInto":[makeQuery(id+"F3.boolean.opBoolean","SPLIT",FACE,{"disambiguationData":[TD([subQ3])],"derivedFrom":subQ2})]}),makeQuery(id+"F3.boolean.opBoolean","SPLIT",FACE,{"disambiguationData":[TD([subQ3])],"derivedFrom":subQ4})],"blendedInto":[makeQuery(id+"F3.boolean.opBoolean","SPLIT",FACE,{"disambiguationData":[TD([subQ3])],"derivedFrom":subQ4})]});}
            var Q11;
            {var subQ0=makeQuery(id+"F3.opExtrude","SWEPT_FACE",FACE,{"disambiguationData":[OSD([sQuery(id+"F2.wireOp",EDGE,"E16.1.1")])]});Q11=makeQuery(id+"F6.opChamfer","BLEND_EDGE",EDGE,{"blendedFrom":[makeQuery(id+"F3.boolean.opBoolean","INTERSECT",EDGE,{"derivedFrom":[makeQuery(id+"F1.opRevolve","SWEPT_FACE",FACE,{"disambiguationData":[OSD([sQuery(id+"F0.wireOp",EDGE,"E10")])]}),subQ0]}),makeQuery(id+"F3.boolean.opBoolean","SPLIT",FACE,{"disambiguationData":[TD([makeQuery(id+"F3.opExtrude","SWEPT_FACE",FACE,{"disambiguationData":[OSD([sQuery(id+"F2.wireOp",EDGE,"E13")])]})])],"derivedFrom":makeQuery(id+"F1.opRevolve","SWEPT_FACE",FACE,{"disambiguationData":[OSD([sQuery(id+"F0.wireOp",EDGE,"E6")])]})})],"blendedInto":[makeQuery(id+"F3.boolean.opBoolean","SPLIT",FACE,{"disambiguationData":[TD([makeQuery(id+"F3.opExtrude","SWEPT_FACE",FACE,{"disambiguationData":[OSD([sQuery(id+"F2.wireOp",EDGE,"E13")])]})])],"derivedFrom":makeQuery(id+"F1.opRevolve","SWEPT_FACE",FACE,{"disambiguationData":[OSD([sQuery(id+"F0.wireOp",EDGE,"E6")])]})})]});}
            chamfer(context, id + "F13", {"entities" : qUnion([Q0, Q1, Q2, Q3, Q4, Q5, Q6, Q7, Q8, Q9, Q10, Q11]), "width" : 1 * mm, "tangentPropagation" : true});
        }
    });
